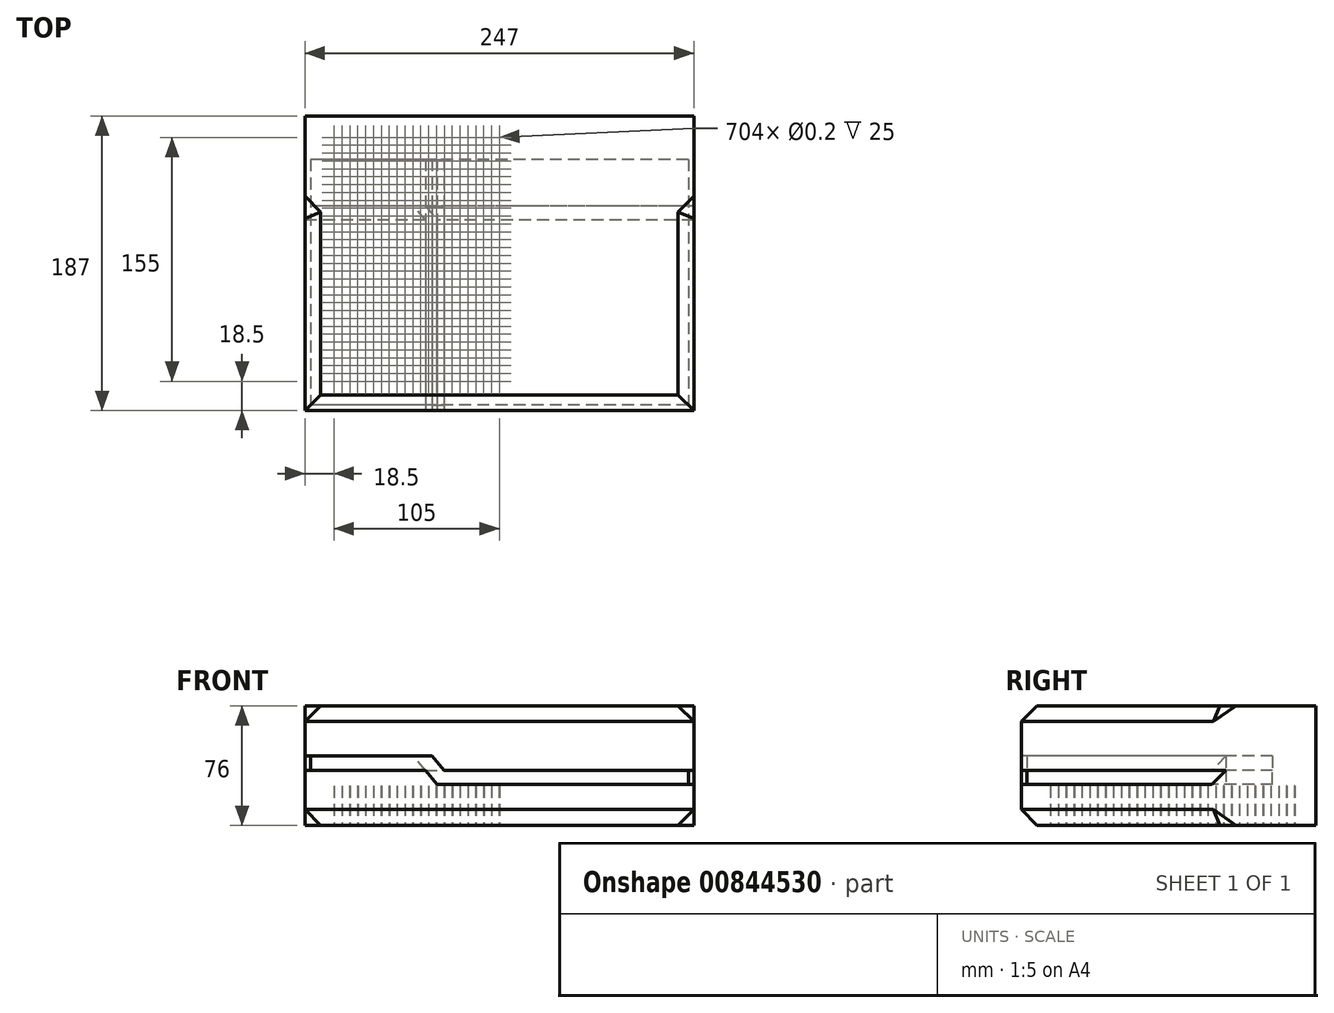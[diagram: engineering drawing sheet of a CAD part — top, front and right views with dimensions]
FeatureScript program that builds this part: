
annotation { "Feature Type Name" : "Feature", "Feature Type Description" : "" }
export const myFeature = defineFeature(function(context is Context, id is Id, definition is map)
    precondition{}
    {
        {
            var Q0;
            Q0=qCreatedBy(makeId("Top.planeOp"),FACE);
            var sketch = newSketch(context, id + "F0", { "sketchPlane" : qUnion([Q0])});
            skLineSegment(sketch, "E0.bottom", {"start": v(123.5, -93.5) * mm, "end": v(-123.5, -93.5) * mm});
            skLineSegment(sketch, "E0.top", {"start": v(123.5, 93.5) * mm, "end": v(-123.5, 93.5) * mm});
            skLineSegment(sketch, "E0.left", {"start": v(123.5, -93.5) * mm, "end": v(123.5, 93.5) * mm});
            skLineSegment(sketch, "E0.right", {"start": v(-123.5, -93.5) * mm, "end": v(-123.5, 93.5) * mm});
            skPoint(sketch, "E0.middle", {"position": v(0, 0) * mm});
            skSolve(sketch);
        }
        {
            var Q0;
            Q0 = qSketchRegion(id + "F0", true);
            extrude(context, id + "F1", {"entities" : qUnion([Q0]), "depth" : 76 * mm, "offsetDistance" : 25 * mm});
        }
        {
            var Q0;
            Q0=makeQuery(id+"F1.opExtrude","CAP_EDGE",EDGE,{"disambiguationData":[OSD([sQuery(id+"F0.wireOp",EDGE,"E0.right")])],"isStart":false});
            var Q1;
            Q1=makeQuery(id+"F1.opExtrude","CAP_EDGE",EDGE,{"disambiguationData":[OSD([sQuery(id+"F0.wireOp",EDGE,"E0.left")])],"isStart":false});
            var Q2;
            Q2=makeQuery(id+"F1.opExtrude","CAP_EDGE",EDGE,{"disambiguationData":[OSD([sQuery(id+"F0.wireOp",EDGE,"E0.right")])],"isStart":true});
            var Q3;
            Q3=makeQuery(id+"F1.opExtrude","CAP_EDGE",EDGE,{"disambiguationData":[OSD([sQuery(id+"F0.wireOp",EDGE,"E0.left")])],"isStart":true});
            var Q4;
            Q4=makeQuery(id+"F1.opExtrude","CAP_EDGE",EDGE,{"disambiguationData":[OSD([sQuery(id+"F0.wireOp",EDGE,"E0.bottom")])],"isStart":false});
            var Q5;
            Q5=makeQuery(id+"F1.opExtrude","CAP_EDGE",EDGE,{"disambiguationData":[OSD([sQuery(id+"F0.wireOp",EDGE,"E0.bottom")])],"isStart":true});
            chamfer(context, id + "F2", {"entities" : qUnion([Q0, Q1, Q2, Q3, Q4, Q5]), "width" : 10 * mm, "tangentPropagation" : true});
        }
        {
            var Q0;
            Q0=makeQuery(id+"F1.opExtrude","SWEPT_FACE",FACE,{"disambiguationData":[OSD([sQuery(id+"F0.wireOp",EDGE,"E0.top")])]});
            var sketch = newSketch(context, id + "F3", { "sketchPlane" : qUnion([Q0])});
            skLineSegment(sketch, "E1", {"start": v(-123.5, 76) * mm, "end": v(-113.5, 76) * mm});
            skLineSegment(sketch, "E2", {"start": v(-113.5, 76) * mm, "end": v(-123.5, 66) * mm});
            skLineSegment(sketch, "E3", {"start": v(-123.5, 66) * mm, "end": v(-123.5, 76) * mm});
            skLineSegment(sketch, "E4", {"start": v(-123.5, 10) * mm, "end": v(-113.5, 0) * mm});
            skLineSegment(sketch, "E5", {"start": v(-113.5, 0) * mm, "end": v(-123.5, 0) * mm});
            skLineSegment(sketch, "E6", {"start": v(-123.5, 0) * mm, "end": v(-123.5, 10) * mm});
            skLineSegment(sketch, "E7", {"start": v(113.5, 76) * mm, "end": v(123.5, 76) * mm});
            skLineSegment(sketch, "E8", {"start": v(123.5, 76) * mm, "end": v(123.5, 66) * mm});
            skLineSegment(sketch, "E9", {"start": v(123.5, 66) * mm, "end": v(113.5, 76) * mm});
            skLineSegment(sketch, "E10", {"start": v(113.5, 0) * mm, "end": v(123.5, 0) * mm});
            skLineSegment(sketch, "E11", {"start": v(123.5, 0) * mm, "end": v(123.5, 10) * mm});
            skLineSegment(sketch, "E12", {"start": v(123.5, 10) * mm, "end": v(113.5, 0) * mm});
            skSolve(sketch);
        }
        {
            var Q0;
            Q0 = qSketchRegion(id + "F3", true);
            extrude(context, id + "F4", {"entities" : qUnion([Q0]), "operationType" : NewBodyOperationType.ADD, "oppositeDirection" : true, "depth" : 75 * mm, "offsetDistance" : 25 * mm});
        }
        {
            var Q0;
            Q0=makeQuery(id+"F4.opExtrude","CAP_EDGE",EDGE,{"disambiguationData":[OSD([sQuery(id+"F3.wireOp",EDGE,"E6")])],"isStart":false});
            var Q1;
            Q1=makeQuery(id+"F4.opExtrude","CAP_EDGE",EDGE,{"disambiguationData":[OSD([sQuery(id+"F3.wireOp",EDGE,"E3")])],"isStart":false});
            var Q2;
            Q2=makeQuery(id+"F4.opExtrude","CAP_EDGE",EDGE,{"disambiguationData":[OSD([sQuery(id+"F3.wireOp",EDGE,"E11")])],"isStart":false});
            var Q3;
            Q3=makeQuery(id+"F4.opExtrude","CAP_EDGE",EDGE,{"disambiguationData":[OSD([sQuery(id+"F3.wireOp",EDGE,"E8")])],"isStart":false});
            chamfer(context, id + "F5", {"entities" : qUnion([Q0, Q1, Q2, Q3]), "width" : 10 * mm, "tangentPropagation" : true});
        }
        {
            var Q0;
            Q0=makeQuery(id+"F5.opChamfer","BLEND_EDGE",EDGE,{"blendedFrom":[makeQuery(id+"F4.opExtrude","CAP_EDGE",EDGE,{"disambiguationData":[OSD([sQuery(id+"F3.wireOp",EDGE,"E6")])],"isStart":false}),makeQuery(id+"F4.boolean.opBoolean","MERGE",FACE,{"derivedFrom":[makeQuery(id+"F1.opExtrude","CAP_FACE",FACE,{"disambiguationData":[OSD([sQuery(id+"F0.wireOp",EDGE,"E0.bottom"),sQuery(id+"F0.wireOp",EDGE,"E0.top"),sQuery(id+"F0.wireOp",EDGE,"E0.left"),sQuery(id+"F0.wireOp",EDGE,"E0.right")])],"isStart":true}),makeQuery(id+"F4.opExtrude","SWEPT_FACE",FACE,{"disambiguationData":[OSD([sQuery(id+"F3.wireOp",EDGE,"E5")])]}),makeQuery(id+"F4.opExtrude","SWEPT_FACE",FACE,{"disambiguationData":[OSD([sQuery(id+"F3.wireOp",EDGE,"E10")])]})]})],"blendedInto":[makeQuery(id+"F4.boolean.opBoolean","MERGE",FACE,{"derivedFrom":[makeQuery(id+"F1.opExtrude","CAP_FACE",FACE,{"disambiguationData":[OSD([sQuery(id+"F0.wireOp",EDGE,"E0.bottom"),sQuery(id+"F0.wireOp",EDGE,"E0.top"),sQuery(id+"F0.wireOp",EDGE,"E0.left"),sQuery(id+"F0.wireOp",EDGE,"E0.right")])],"isStart":true}),makeQuery(id+"F4.opExtrude","SWEPT_FACE",FACE,{"disambiguationData":[OSD([sQuery(id+"F3.wireOp",EDGE,"E5")])]}),makeQuery(id+"F4.opExtrude","SWEPT_FACE",FACE,{"disambiguationData":[OSD([sQuery(id+"F3.wireOp",EDGE,"E10")])]})]})]});
            var Q1;
            Q1=makeQuery(id+"F5.opChamfer","BLEND_EDGE",EDGE,{"blendedFrom":[makeQuery(id+"F4.opExtrude","CAP_EDGE",EDGE,{"disambiguationData":[OSD([sQuery(id+"F3.wireOp",EDGE,"E3")])],"isStart":false}),makeQuery(id+"F4.boolean.opBoolean","MERGE",FACE,{"derivedFrom":[makeQuery(id+"F1.opExtrude","CAP_FACE",FACE,{"disambiguationData":[OSD([sQuery(id+"F0.wireOp",EDGE,"E0.bottom"),sQuery(id+"F0.wireOp",EDGE,"E0.top"),sQuery(id+"F0.wireOp",EDGE,"E0.left"),sQuery(id+"F0.wireOp",EDGE,"E0.right")])],"isStart":false}),makeQuery(id+"F4.opExtrude","SWEPT_FACE",FACE,{"disambiguationData":[OSD([sQuery(id+"F3.wireOp",EDGE,"E1")])]}),makeQuery(id+"F4.opExtrude","SWEPT_FACE",FACE,{"disambiguationData":[OSD([sQuery(id+"F3.wireOp",EDGE,"E7")])]})]})],"blendedInto":[makeQuery(id+"F4.boolean.opBoolean","MERGE",FACE,{"derivedFrom":[makeQuery(id+"F1.opExtrude","CAP_FACE",FACE,{"disambiguationData":[OSD([sQuery(id+"F0.wireOp",EDGE,"E0.bottom"),sQuery(id+"F0.wireOp",EDGE,"E0.top"),sQuery(id+"F0.wireOp",EDGE,"E0.left"),sQuery(id+"F0.wireOp",EDGE,"E0.right")])],"isStart":false}),makeQuery(id+"F4.opExtrude","SWEPT_FACE",FACE,{"disambiguationData":[OSD([sQuery(id+"F3.wireOp",EDGE,"E1")])]}),makeQuery(id+"F4.opExtrude","SWEPT_FACE",FACE,{"disambiguationData":[OSD([sQuery(id+"F3.wireOp",EDGE,"E7")])]})]})]});
            var Q2;
            Q2=makeQuery(id+"F5.opChamfer","BLEND_EDGE",EDGE,{"blendedFrom":[makeQuery(id+"F4.opExtrude","CAP_EDGE",EDGE,{"disambiguationData":[OSD([sQuery(id+"F3.wireOp",EDGE,"E11")])],"isStart":false}),makeQuery(id+"F4.boolean.opBoolean","MERGE",FACE,{"derivedFrom":[makeQuery(id+"F1.opExtrude","CAP_FACE",FACE,{"disambiguationData":[OSD([sQuery(id+"F0.wireOp",EDGE,"E0.bottom"),sQuery(id+"F0.wireOp",EDGE,"E0.top"),sQuery(id+"F0.wireOp",EDGE,"E0.left"),sQuery(id+"F0.wireOp",EDGE,"E0.right")])],"isStart":true}),makeQuery(id+"F4.opExtrude","SWEPT_FACE",FACE,{"disambiguationData":[OSD([sQuery(id+"F3.wireOp",EDGE,"E5")])]}),makeQuery(id+"F4.opExtrude","SWEPT_FACE",FACE,{"disambiguationData":[OSD([sQuery(id+"F3.wireOp",EDGE,"E10")])]})]})],"blendedInto":[makeQuery(id+"F4.boolean.opBoolean","MERGE",FACE,{"derivedFrom":[makeQuery(id+"F1.opExtrude","CAP_FACE",FACE,{"disambiguationData":[OSD([sQuery(id+"F0.wireOp",EDGE,"E0.bottom"),sQuery(id+"F0.wireOp",EDGE,"E0.top"),sQuery(id+"F0.wireOp",EDGE,"E0.left"),sQuery(id+"F0.wireOp",EDGE,"E0.right")])],"isStart":true}),makeQuery(id+"F4.opExtrude","SWEPT_FACE",FACE,{"disambiguationData":[OSD([sQuery(id+"F3.wireOp",EDGE,"E5")])]}),makeQuery(id+"F4.opExtrude","SWEPT_FACE",FACE,{"disambiguationData":[OSD([sQuery(id+"F3.wireOp",EDGE,"E10")])]})]})]});
            var Q3;
            Q3=makeQuery(id+"F5.opChamfer","BLEND_EDGE",EDGE,{"blendedFrom":[makeQuery(id+"F4.opExtrude","CAP_EDGE",EDGE,{"disambiguationData":[OSD([sQuery(id+"F3.wireOp",EDGE,"E8")])],"isStart":false}),makeQuery(id+"F4.boolean.opBoolean","MERGE",FACE,{"derivedFrom":[makeQuery(id+"F1.opExtrude","CAP_FACE",FACE,{"disambiguationData":[OSD([sQuery(id+"F0.wireOp",EDGE,"E0.bottom"),sQuery(id+"F0.wireOp",EDGE,"E0.top"),sQuery(id+"F0.wireOp",EDGE,"E0.left"),sQuery(id+"F0.wireOp",EDGE,"E0.right")])],"isStart":false}),makeQuery(id+"F4.opExtrude","SWEPT_FACE",FACE,{"disambiguationData":[OSD([sQuery(id+"F3.wireOp",EDGE,"E1")])]}),makeQuery(id+"F4.opExtrude","SWEPT_FACE",FACE,{"disambiguationData":[OSD([sQuery(id+"F3.wireOp",EDGE,"E7")])]})]})],"blendedInto":[makeQuery(id+"F4.boolean.opBoolean","MERGE",FACE,{"derivedFrom":[makeQuery(id+"F1.opExtrude","CAP_FACE",FACE,{"disambiguationData":[OSD([sQuery(id+"F0.wireOp",EDGE,"E0.bottom"),sQuery(id+"F0.wireOp",EDGE,"E0.top"),sQuery(id+"F0.wireOp",EDGE,"E0.left"),sQuery(id+"F0.wireOp",EDGE,"E0.right")])],"isStart":false}),makeQuery(id+"F4.opExtrude","SWEPT_FACE",FACE,{"disambiguationData":[OSD([sQuery(id+"F3.wireOp",EDGE,"E1")])]}),makeQuery(id+"F4.opExtrude","SWEPT_FACE",FACE,{"disambiguationData":[OSD([sQuery(id+"F3.wireOp",EDGE,"E7")])]})]})]});
            chamfer(context, id + "F6", {"entities" : qUnion([Q0, Q1, Q2, Q3]), "width" : 10 * mm, "tangentPropagation" : true});
        }
        {
            var Q0;
            Q0=makeQuery(id+"F1.opExtrude","SWEPT_FACE",FACE,{"disambiguationData":[OSD([sQuery(id+"F0.wireOp",EDGE,"E0.bottom")])]});
            var sketch = newSketch(context, id + "F7", { "sketchPlane" : qUnion([Q0])});
            skLineSegment(sketch, "E13", {"start": v(123.5, 10) * mm, "end": v(123.5, 26) * mm});
            skLineSegment(sketch, "E14", {"start": v(123.5, 26) * mm, "end": v(-39.52, 26) * mm});
            skLineSegment(sketch, "E15.0", {"start": v(123.5, 35) * mm, "end": v(-35.3, 35) * mm});
            skLineSegment(sketch, "E16", {"start": v(-47.02, 35) * mm, "end": v(-123.5, 35) * mm});
            skLineSegment(sketch, "E17.0", {"start": v(-42.8, 44) * mm, "end": v(-123.5, 44) * mm});
            skLineSegment(sketch, "E18", {"start": v(-39.52, 26) * mm, "end": v(-47.02, 35) * mm});
            skLineSegment(sketch, "E19", {"start": v(-42.8, 44) * mm, "end": v(-35.3, 35) * mm});
            skLineSegment(sketch, "E20", {"start": v(123.5, 26) * mm, "end": v(123.5, 35) * mm});
            skLineSegment(sketch, "E21", {"start": v(-123.5, 44) * mm, "end": v(-123.5, 35) * mm});
            skSolve(sketch);
        }
        {
            var Q0;
            Q0 = qSketchRegion(id + "F7", true);
            extrude(context, id + "F8", {"entities" : qUnion([Q0]), "operationType" : NewBodyOperationType.REMOVE, "oppositeDirection" : true, "depth" : 130 * mm, "offsetDistance" : 25 * mm});
        }
        {
            var Q0;
            Q0=makeQuery(id+"F8.boolean.opBoolean","COPY",EDGE,{"derivedFrom":makeQuery(id+"F8.opExtrude","CAP_EDGE",EDGE,{"disambiguationData":[OSD([sQuery(id+"F7.wireOp",EDGE,"E16")])],"isStart":false})});
            var Q1;
            Q1=makeQuery(id+"F8.boolean.opBoolean","COPY",EDGE,{"derivedFrom":makeQuery(id+"F8.opExtrude","CAP_EDGE",EDGE,{"disambiguationData":[OSD([sQuery(id+"F7.wireOp",EDGE,"E14")])],"isStart":false})});
            chamfer(context, id + "F9", {"entities" : qUnion([Q0, Q1]), "width" : 9 * mm, "tangentPropagation" : true});
        }
        {
            var Q0;
            Q0=qCreatedBy(makeId("Front.planeOp"),FACE);
            cPlane(context, id + "F10", {"entities" : qUnion([Q0]), "cplaneType" : CPlaneType.OFFSET, "offset" : 90 * mm, "width" : 150 * mm, "height" : 150 * mm});
        }
        {
            var Q0;
            Q0=qCreatedBy(id+"F10.planeOp",FACE);
            var sketch = newSketch(context, id + "F11", { "sketchPlane" : qUnion([Q0])});
            skLineSegment(sketch, "E22", {"start": v(123.5, 26) * mm, "end": v(-39.52, 26) * mm});
            skLineSegment(sketch, "E23.0", {"start": v(123.5, 35) * mm, "end": v(-35.3, 35) * mm});
            skLineSegment(sketch, "E24", {"start": v(-47.02, 35) * mm, "end": v(-123.5, 35) * mm});
            skLineSegment(sketch, "E25.0", {"start": v(-42.8, 44) * mm, "end": v(-123.5, 44) * mm});
            skLineSegment(sketch, "E26", {"start": v(-39.52, 26) * mm, "end": v(-47.02, 35) * mm});
            skLineSegment(sketch, "E27", {"start": v(-42.8, 44) * mm, "end": v(-35.3, 35) * mm});
            skLineSegment(sketch, "E28", {"start": v(123.5, 26) * mm, "end": v(123.5, 35) * mm});
            skLineSegment(sketch, "E29", {"start": v(-123.5, 44) * mm, "end": v(-123.5, 35) * mm});
            skLineSegment(sketch, "E30.0", {"start": v(120, 26) * mm, "end": v(120, 35) * mm});
            skLineSegment(sketch, "E31.0", {"start": v(-120, 44) * mm, "end": v(-120, 35) * mm});
            skSolve(sketch);
        }
        {
            var Q0;
            {var subQ0=sQuery(id+"F11.wireOp",EDGE,"E26");Q0=makeQuery(id+"F11.imprint","IMPRINT",FACE,{"disambiguationData":[TD([[makeQuery(id+"F11.imprint","IMPRINT",EDGE,{"derivedFrom":subQ0}),-1.0]])]});}
            extrude(context, id + "F12", {"entities" : qUnion([Q0]), "oppositeDirection" : true, "depth" : 156 * mm, "offsetDistance" : 25 * mm});
        }
        {
            var Q0;
            Q0=makeQuery(id+"F4.boolean.opBoolean","MERGE",FACE,{"derivedFrom":[makeQuery(id+"F1.opExtrude","CAP_FACE",FACE,{"disambiguationData":[OSD([sQuery(id+"F0.wireOp",EDGE,"E0.bottom"),sQuery(id+"F0.wireOp",EDGE,"E0.top"),sQuery(id+"F0.wireOp",EDGE,"E0.left"),sQuery(id+"F0.wireOp",EDGE,"E0.right")])],"isStart":true}),makeQuery(id+"F4.opExtrude","SWEPT_FACE",FACE,{"disambiguationData":[OSD([sQuery(id+"F3.wireOp",EDGE,"E5")])]}),makeQuery(id+"F4.opExtrude","SWEPT_FACE",FACE,{"disambiguationData":[OSD([sQuery(id+"F3.wireOp",EDGE,"E10")])]})]});
            var sketch = newSketch(context, id + "F13", { "sketchPlane" : qUnion([Q0])});
            skCircle(sketch, "E32", {"center": v(0, 0) * mm, "radius": 0.1 * mm});
            skCircle(sketch, "E33.0.1.0", {"center": v(0, 5) * mm, "radius": 0.1 * mm});
            skCircle(sketch, "E33.0.2.0", {"center": v(0, 10) * mm, "radius": 0.1 * mm});
            skCircle(sketch, "E33.0.3.0", {"center": v(0, 15) * mm, "radius": 0.1 * mm});
            skCircle(sketch, "E33.0.4.0", {"center": v(0, 20) * mm, "radius": 0.1 * mm});
            skCircle(sketch, "E33.0.5.0", {"center": v(0, 25) * mm, "radius": 0.1 * mm});
            skCircle(sketch, "E33.0.6.0", {"center": v(0, 30) * mm, "radius": 0.1 * mm});
            skCircle(sketch, "E33.0.7.0", {"center": v(0, 35) * mm, "radius": 0.1 * mm});
            skCircle(sketch, "E33.0.8.0", {"center": v(0, 40) * mm, "radius": 0.1 * mm});
            skCircle(sketch, "E33.0.9.0", {"center": v(0, 45) * mm, "radius": 0.1 * mm});
            skCircle(sketch, "E33.0.10.0", {"center": v(0, 50) * mm, "radius": 0.1 * mm});
            skCircle(sketch, "E33.0.11.0", {"center": v(0, 55) * mm, "radius": 0.1 * mm});
            skCircle(sketch, "E33.0.12.0", {"center": v(0, 60) * mm, "radius": 0.1 * mm});
            skCircle(sketch, "E33.0.13.0", {"center": v(0, 65) * mm, "radius": 0.1 * mm});
            skCircle(sketch, "E33.0.14.0", {"center": v(0, 70) * mm, "radius": 0.1 * mm});
            skCircle(sketch, "E33.1.0.0", {"center": v(-5, 0) * mm, "radius": 0.1 * mm});
            skCircle(sketch, "E33.1.1.0", {"center": v(-5, 5) * mm, "radius": 0.1 * mm});
            skCircle(sketch, "E33.1.2.0", {"center": v(-5, 10) * mm, "radius": 0.1 * mm});
            skCircle(sketch, "E33.1.3.0", {"center": v(-5, 15) * mm, "radius": 0.1 * mm});
            skCircle(sketch, "E33.1.4.0", {"center": v(-5, 20) * mm, "radius": 0.1 * mm});
            skCircle(sketch, "E33.1.5.0", {"center": v(-5, 25) * mm, "radius": 0.1 * mm});
            skCircle(sketch, "E33.1.6.0", {"center": v(-5, 30) * mm, "radius": 0.1 * mm});
            skCircle(sketch, "E33.1.7.0", {"center": v(-5, 35) * mm, "radius": 0.1 * mm});
            skCircle(sketch, "E33.1.8.0", {"center": v(-5, 40) * mm, "radius": 0.1 * mm});
            skCircle(sketch, "E33.1.9.0", {"center": v(-5, 45) * mm, "radius": 0.1 * mm});
            skCircle(sketch, "E33.1.10.0", {"center": v(-5, 50) * mm, "radius": 0.1 * mm});
            skCircle(sketch, "E33.1.11.0", {"center": v(-5, 55) * mm, "radius": 0.1 * mm});
            skCircle(sketch, "E33.1.12.0", {"center": v(-5, 60) * mm, "radius": 0.1 * mm});
            skCircle(sketch, "E33.1.13.0", {"center": v(-5, 65) * mm, "radius": 0.1 * mm});
            skCircle(sketch, "E33.1.14.0", {"center": v(-5, 70) * mm, "radius": 0.1 * mm});
            skCircle(sketch, "E33.2.0.0", {"center": v(-10, 0) * mm, "radius": 0.1 * mm});
            skCircle(sketch, "E33.2.1.0", {"center": v(-10, 5) * mm, "radius": 0.1 * mm});
            skCircle(sketch, "E33.2.2.0", {"center": v(-10, 10) * mm, "radius": 0.1 * mm});
            skCircle(sketch, "E33.2.3.0", {"center": v(-10, 15) * mm, "radius": 0.1 * mm});
            skCircle(sketch, "E33.2.4.0", {"center": v(-10, 20) * mm, "radius": 0.1 * mm});
            skCircle(sketch, "E33.2.5.0", {"center": v(-10, 25) * mm, "radius": 0.1 * mm});
            skCircle(sketch, "E33.2.6.0", {"center": v(-10, 30) * mm, "radius": 0.1 * mm});
            skCircle(sketch, "E33.2.7.0", {"center": v(-10, 35) * mm, "radius": 0.1 * mm});
            skCircle(sketch, "E33.2.8.0", {"center": v(-10, 40) * mm, "radius": 0.1 * mm});
            skCircle(sketch, "E33.2.9.0", {"center": v(-10, 45) * mm, "radius": 0.1 * mm});
            skCircle(sketch, "E33.2.10.0", {"center": v(-10, 50) * mm, "radius": 0.1 * mm});
            skCircle(sketch, "E33.2.11.0", {"center": v(-10, 55) * mm, "radius": 0.1 * mm});
            skCircle(sketch, "E33.2.12.0", {"center": v(-10, 60) * mm, "radius": 0.1 * mm});
            skCircle(sketch, "E33.2.13.0", {"center": v(-10, 65) * mm, "radius": 0.1 * mm});
            skCircle(sketch, "E33.2.14.0", {"center": v(-10, 70) * mm, "radius": 0.1 * mm});
            skCircle(sketch, "E33.3.0.0", {"center": v(-15, 0) * mm, "radius": 0.1 * mm});
            skCircle(sketch, "E33.3.1.0", {"center": v(-15, 5) * mm, "radius": 0.1 * mm});
            skCircle(sketch, "E33.3.2.0", {"center": v(-15, 10) * mm, "radius": 0.1 * mm});
            skCircle(sketch, "E33.3.3.0", {"center": v(-15, 15) * mm, "radius": 0.1 * mm});
            skCircle(sketch, "E33.3.4.0", {"center": v(-15, 20) * mm, "radius": 0.1 * mm});
            skCircle(sketch, "E33.3.5.0", {"center": v(-15, 25) * mm, "radius": 0.1 * mm});
            skCircle(sketch, "E33.3.6.0", {"center": v(-15, 30) * mm, "radius": 0.1 * mm});
            skCircle(sketch, "E33.3.7.0", {"center": v(-15, 35) * mm, "radius": 0.1 * mm});
            skCircle(sketch, "E33.3.8.0", {"center": v(-15, 40) * mm, "radius": 0.1 * mm});
            skCircle(sketch, "E33.3.9.0", {"center": v(-15, 45) * mm, "radius": 0.1 * mm});
            skCircle(sketch, "E33.3.10.0", {"center": v(-15, 50) * mm, "radius": 0.1 * mm});
            skCircle(sketch, "E33.3.11.0", {"center": v(-15, 55) * mm, "radius": 0.1 * mm});
            skCircle(sketch, "E33.3.12.0", {"center": v(-15, 60) * mm, "radius": 0.1 * mm});
            skCircle(sketch, "E33.3.13.0", {"center": v(-15, 65) * mm, "radius": 0.1 * mm});
            skCircle(sketch, "E33.3.14.0", {"center": v(-15, 70) * mm, "radius": 0.1 * mm});
            skCircle(sketch, "E33.4.0.0", {"center": v(-20, 0) * mm, "radius": 0.1 * mm});
            skCircle(sketch, "E33.4.1.0", {"center": v(-20, 5) * mm, "radius": 0.1 * mm});
            skCircle(sketch, "E33.4.2.0", {"center": v(-20, 10) * mm, "radius": 0.1 * mm});
            skCircle(sketch, "E33.4.3.0", {"center": v(-20, 15) * mm, "radius": 0.1 * mm});
            skCircle(sketch, "E33.4.4.0", {"center": v(-20, 20) * mm, "radius": 0.1 * mm});
            skCircle(sketch, "E33.4.5.0", {"center": v(-20, 25) * mm, "radius": 0.1 * mm});
            skCircle(sketch, "E33.4.6.0", {"center": v(-20, 30) * mm, "radius": 0.1 * mm});
            skCircle(sketch, "E33.4.7.0", {"center": v(-20, 35) * mm, "radius": 0.1 * mm});
            skCircle(sketch, "E33.4.8.0", {"center": v(-20, 40) * mm, "radius": 0.1 * mm});
            skCircle(sketch, "E33.4.9.0", {"center": v(-20, 45) * mm, "radius": 0.1 * mm});
            skCircle(sketch, "E33.4.10.0", {"center": v(-20, 50) * mm, "radius": 0.1 * mm});
            skCircle(sketch, "E33.4.11.0", {"center": v(-20, 55) * mm, "radius": 0.1 * mm});
            skCircle(sketch, "E33.4.12.0", {"center": v(-20, 60) * mm, "radius": 0.1 * mm});
            skCircle(sketch, "E33.4.13.0", {"center": v(-20, 65) * mm, "radius": 0.1 * mm});
            skCircle(sketch, "E33.4.14.0", {"center": v(-20, 70) * mm, "radius": 0.1 * mm});
            skCircle(sketch, "E33.5.0.0", {"center": v(-25, 0) * mm, "radius": 0.1 * mm});
            skCircle(sketch, "E33.5.1.0", {"center": v(-25, 5) * mm, "radius": 0.1 * mm});
            skCircle(sketch, "E33.5.2.0", {"center": v(-25, 10) * mm, "radius": 0.1 * mm});
            skCircle(sketch, "E33.5.3.0", {"center": v(-25, 15) * mm, "radius": 0.1 * mm});
            skCircle(sketch, "E33.5.4.0", {"center": v(-25, 20) * mm, "radius": 0.1 * mm});
            skCircle(sketch, "E33.5.5.0", {"center": v(-25, 25) * mm, "radius": 0.1 * mm});
            skCircle(sketch, "E33.5.6.0", {"center": v(-25, 30) * mm, "radius": 0.1 * mm});
            skCircle(sketch, "E33.5.7.0", {"center": v(-25, 35) * mm, "radius": 0.1 * mm});
            skCircle(sketch, "E33.5.8.0", {"center": v(-25, 40) * mm, "radius": 0.1 * mm});
            skCircle(sketch, "E33.5.9.0", {"center": v(-25, 45) * mm, "radius": 0.1 * mm});
            skCircle(sketch, "E33.5.10.0", {"center": v(-25, 50) * mm, "radius": 0.1 * mm});
            skCircle(sketch, "E33.5.11.0", {"center": v(-25, 55) * mm, "radius": 0.1 * mm});
            skCircle(sketch, "E33.5.12.0", {"center": v(-25, 60) * mm, "radius": 0.1 * mm});
            skCircle(sketch, "E33.5.13.0", {"center": v(-25, 65) * mm, "radius": 0.1 * mm});
            skCircle(sketch, "E33.5.14.0", {"center": v(-25, 70) * mm, "radius": 0.1 * mm});
            skCircle(sketch, "E33.6.0.0", {"center": v(-30, 0) * mm, "radius": 0.1 * mm});
            skCircle(sketch, "E33.6.1.0", {"center": v(-30, 5) * mm, "radius": 0.1 * mm});
            skCircle(sketch, "E33.6.2.0", {"center": v(-30, 10) * mm, "radius": 0.1 * mm});
            skCircle(sketch, "E33.6.3.0", {"center": v(-30, 15) * mm, "radius": 0.1 * mm});
            skCircle(sketch, "E33.6.4.0", {"center": v(-30, 20) * mm, "radius": 0.1 * mm});
            skCircle(sketch, "E33.6.5.0", {"center": v(-30, 25) * mm, "radius": 0.1 * mm});
            skCircle(sketch, "E33.6.6.0", {"center": v(-30, 30) * mm, "radius": 0.1 * mm});
            skCircle(sketch, "E33.6.7.0", {"center": v(-30, 35) * mm, "radius": 0.1 * mm});
            skCircle(sketch, "E33.6.8.0", {"center": v(-30, 40) * mm, "radius": 0.1 * mm});
            skCircle(sketch, "E33.6.9.0", {"center": v(-30, 45) * mm, "radius": 0.1 * mm});
            skCircle(sketch, "E33.6.10.0", {"center": v(-30, 50) * mm, "radius": 0.1 * mm});
            skCircle(sketch, "E33.6.11.0", {"center": v(-30, 55) * mm, "radius": 0.1 * mm});
            skCircle(sketch, "E33.6.12.0", {"center": v(-30, 60) * mm, "radius": 0.1 * mm});
            skCircle(sketch, "E33.6.13.0", {"center": v(-30, 65) * mm, "radius": 0.1 * mm});
            skCircle(sketch, "E33.6.14.0", {"center": v(-30, 70) * mm, "radius": 0.1 * mm});
            skCircle(sketch, "E33.7.0.0", {"center": v(-35, 0) * mm, "radius": 0.1 * mm});
            skCircle(sketch, "E33.7.1.0", {"center": v(-35, 5) * mm, "radius": 0.1 * mm});
            skCircle(sketch, "E33.7.2.0", {"center": v(-35, 10) * mm, "radius": 0.1 * mm});
            skCircle(sketch, "E33.7.3.0", {"center": v(-35, 15) * mm, "radius": 0.1 * mm});
            skCircle(sketch, "E33.7.4.0", {"center": v(-35, 20) * mm, "radius": 0.1 * mm});
            skCircle(sketch, "E33.7.5.0", {"center": v(-35, 25) * mm, "radius": 0.1 * mm});
            skCircle(sketch, "E33.7.6.0", {"center": v(-35, 30) * mm, "radius": 0.1 * mm});
            skCircle(sketch, "E33.7.7.0", {"center": v(-35, 35) * mm, "radius": 0.1 * mm});
            skCircle(sketch, "E33.7.8.0", {"center": v(-35, 40) * mm, "radius": 0.1 * mm});
            skCircle(sketch, "E33.7.9.0", {"center": v(-35, 45) * mm, "radius": 0.1 * mm});
            skCircle(sketch, "E33.7.10.0", {"center": v(-35, 50) * mm, "radius": 0.1 * mm});
            skCircle(sketch, "E33.7.11.0", {"center": v(-35, 55) * mm, "radius": 0.1 * mm});
            skCircle(sketch, "E33.7.12.0", {"center": v(-35, 60) * mm, "radius": 0.1 * mm});
            skCircle(sketch, "E33.7.13.0", {"center": v(-35, 65) * mm, "radius": 0.1 * mm});
            skCircle(sketch, "E33.7.14.0", {"center": v(-35, 70) * mm, "radius": 0.1 * mm});
            skCircle(sketch, "E33.8.0.0", {"center": v(-40, 0) * mm, "radius": 0.1 * mm});
            skCircle(sketch, "E33.8.1.0", {"center": v(-40, 5) * mm, "radius": 0.1 * mm});
            skCircle(sketch, "E33.8.2.0", {"center": v(-40, 10) * mm, "radius": 0.1 * mm});
            skCircle(sketch, "E33.8.3.0", {"center": v(-40, 15) * mm, "radius": 0.1 * mm});
            skCircle(sketch, "E33.8.4.0", {"center": v(-40, 20) * mm, "radius": 0.1 * mm});
            skCircle(sketch, "E33.8.5.0", {"center": v(-40, 25) * mm, "radius": 0.1 * mm});
            skCircle(sketch, "E33.8.6.0", {"center": v(-40, 30) * mm, "radius": 0.1 * mm});
            skCircle(sketch, "E33.8.7.0", {"center": v(-40, 35) * mm, "radius": 0.1 * mm});
            skCircle(sketch, "E33.8.8.0", {"center": v(-40, 40) * mm, "radius": 0.1 * mm});
            skCircle(sketch, "E33.8.9.0", {"center": v(-40, 45) * mm, "radius": 0.1 * mm});
            skCircle(sketch, "E33.8.10.0", {"center": v(-40, 50) * mm, "radius": 0.1 * mm});
            skCircle(sketch, "E33.8.11.0", {"center": v(-40, 55) * mm, "radius": 0.1 * mm});
            skCircle(sketch, "E33.8.12.0", {"center": v(-40, 60) * mm, "radius": 0.1 * mm});
            skCircle(sketch, "E33.8.13.0", {"center": v(-40, 65) * mm, "radius": 0.1 * mm});
            skCircle(sketch, "E33.8.14.0", {"center": v(-40, 70) * mm, "radius": 0.1 * mm});
            skCircle(sketch, "E33.9.0.0", {"center": v(-45, 0) * mm, "radius": 0.1 * mm});
            skCircle(sketch, "E33.9.1.0", {"center": v(-45, 5) * mm, "radius": 0.1 * mm});
            skCircle(sketch, "E33.9.2.0", {"center": v(-45, 10) * mm, "radius": 0.1 * mm});
            skCircle(sketch, "E33.9.3.0", {"center": v(-45, 15) * mm, "radius": 0.1 * mm});
            skCircle(sketch, "E33.9.4.0", {"center": v(-45, 20) * mm, "radius": 0.1 * mm});
            skCircle(sketch, "E33.9.5.0", {"center": v(-45, 25) * mm, "radius": 0.1 * mm});
            skCircle(sketch, "E33.9.6.0", {"center": v(-45, 30) * mm, "radius": 0.1 * mm});
            skCircle(sketch, "E33.9.7.0", {"center": v(-45, 35) * mm, "radius": 0.1 * mm});
            skCircle(sketch, "E33.9.8.0", {"center": v(-45, 40) * mm, "radius": 0.1 * mm});
            skCircle(sketch, "E33.9.9.0", {"center": v(-45, 45) * mm, "radius": 0.1 * mm});
            skCircle(sketch, "E33.9.10.0", {"center": v(-45, 50) * mm, "radius": 0.1 * mm});
            skCircle(sketch, "E33.9.11.0", {"center": v(-45, 55) * mm, "radius": 0.1 * mm});
            skCircle(sketch, "E33.9.12.0", {"center": v(-45, 60) * mm, "radius": 0.1 * mm});
            skCircle(sketch, "E33.9.13.0", {"center": v(-45, 65) * mm, "radius": 0.1 * mm});
            skCircle(sketch, "E33.9.14.0", {"center": v(-45, 70) * mm, "radius": 0.1 * mm});
            skCircle(sketch, "E33.10.0.0", {"center": v(-50, 0) * mm, "radius": 0.1 * mm});
            skCircle(sketch, "E33.10.1.0", {"center": v(-50, 5) * mm, "radius": 0.1 * mm});
            skCircle(sketch, "E33.10.2.0", {"center": v(-50, 10) * mm, "radius": 0.1 * mm});
            skCircle(sketch, "E33.10.3.0", {"center": v(-50, 15) * mm, "radius": 0.1 * mm});
            skCircle(sketch, "E33.10.4.0", {"center": v(-50, 20) * mm, "radius": 0.1 * mm});
            skCircle(sketch, "E33.10.5.0", {"center": v(-50, 25) * mm, "radius": 0.1 * mm});
            skCircle(sketch, "E33.10.6.0", {"center": v(-50, 30) * mm, "radius": 0.1 * mm});
            skCircle(sketch, "E33.10.7.0", {"center": v(-50, 35) * mm, "radius": 0.1 * mm});
            skCircle(sketch, "E33.10.8.0", {"center": v(-50, 40) * mm, "radius": 0.1 * mm});
            skCircle(sketch, "E33.10.9.0", {"center": v(-50, 45) * mm, "radius": 0.1 * mm});
            skCircle(sketch, "E33.10.10.0", {"center": v(-50, 50) * mm, "radius": 0.1 * mm});
            skCircle(sketch, "E33.10.11.0", {"center": v(-50, 55) * mm, "radius": 0.1 * mm});
            skCircle(sketch, "E33.10.12.0", {"center": v(-50, 60) * mm, "radius": 0.1 * mm});
            skCircle(sketch, "E33.10.13.0", {"center": v(-50, 65) * mm, "radius": 0.1 * mm});
            skCircle(sketch, "E33.10.14.0", {"center": v(-50, 70) * mm, "radius": 0.1 * mm});
            skCircle(sketch, "E33.11.0.0", {"center": v(-55, 0) * mm, "radius": 0.1 * mm});
            skCircle(sketch, "E33.11.1.0", {"center": v(-55, 5) * mm, "radius": 0.1 * mm});
            skCircle(sketch, "E33.11.2.0", {"center": v(-55, 10) * mm, "radius": 0.1 * mm});
            skCircle(sketch, "E33.11.3.0", {"center": v(-55, 15) * mm, "radius": 0.1 * mm});
            skCircle(sketch, "E33.11.4.0", {"center": v(-55, 20) * mm, "radius": 0.1 * mm});
            skCircle(sketch, "E33.11.5.0", {"center": v(-55, 25) * mm, "radius": 0.1 * mm});
            skCircle(sketch, "E33.11.6.0", {"center": v(-55, 30) * mm, "radius": 0.1 * mm});
            skCircle(sketch, "E33.11.7.0", {"center": v(-55, 35) * mm, "radius": 0.1 * mm});
            skCircle(sketch, "E33.11.8.0", {"center": v(-55, 40) * mm, "radius": 0.1 * mm});
            skCircle(sketch, "E33.11.9.0", {"center": v(-55, 45) * mm, "radius": 0.1 * mm});
            skCircle(sketch, "E33.11.10.0", {"center": v(-55, 50) * mm, "radius": 0.1 * mm});
            skCircle(sketch, "E33.11.11.0", {"center": v(-55, 55) * mm, "radius": 0.1 * mm});
            skCircle(sketch, "E33.11.12.0", {"center": v(-55, 60) * mm, "radius": 0.1 * mm});
            skCircle(sketch, "E33.11.13.0", {"center": v(-55, 65) * mm, "radius": 0.1 * mm});
            skCircle(sketch, "E33.11.14.0", {"center": v(-55, 70) * mm, "radius": 0.1 * mm});
            skCircle(sketch, "E33.12.0.0", {"center": v(-60, 0) * mm, "radius": 0.1 * mm});
            skCircle(sketch, "E33.12.1.0", {"center": v(-60, 5) * mm, "radius": 0.1 * mm});
            skCircle(sketch, "E33.12.2.0", {"center": v(-60, 10) * mm, "radius": 0.1 * mm});
            skCircle(sketch, "E33.12.3.0", {"center": v(-60, 15) * mm, "radius": 0.1 * mm});
            skCircle(sketch, "E33.12.4.0", {"center": v(-60, 20) * mm, "radius": 0.1 * mm});
            skCircle(sketch, "E33.12.5.0", {"center": v(-60, 25) * mm, "radius": 0.1 * mm});
            skCircle(sketch, "E33.12.6.0", {"center": v(-60, 30) * mm, "radius": 0.1 * mm});
            skCircle(sketch, "E33.12.7.0", {"center": v(-60, 35) * mm, "radius": 0.1 * mm});
            skCircle(sketch, "E33.12.8.0", {"center": v(-60, 40) * mm, "radius": 0.1 * mm});
            skCircle(sketch, "E33.12.9.0", {"center": v(-60, 45) * mm, "radius": 0.1 * mm});
            skCircle(sketch, "E33.12.10.0", {"center": v(-60, 50) * mm, "radius": 0.1 * mm});
            skCircle(sketch, "E33.12.11.0", {"center": v(-60, 55) * mm, "radius": 0.1 * mm});
            skCircle(sketch, "E33.12.12.0", {"center": v(-60, 60) * mm, "radius": 0.1 * mm});
            skCircle(sketch, "E33.12.13.0", {"center": v(-60, 65) * mm, "radius": 0.1 * mm});
            skCircle(sketch, "E33.12.14.0", {"center": v(-60, 70) * mm, "radius": 0.1 * mm});
            skCircle(sketch, "E33.13.0.0", {"center": v(-65, 0) * mm, "radius": 0.1 * mm});
            skCircle(sketch, "E33.13.1.0", {"center": v(-65, 5) * mm, "radius": 0.1 * mm});
            skCircle(sketch, "E33.13.2.0", {"center": v(-65, 10) * mm, "radius": 0.1 * mm});
            skCircle(sketch, "E33.13.3.0", {"center": v(-65, 15) * mm, "radius": 0.1 * mm});
            skCircle(sketch, "E33.13.4.0", {"center": v(-65, 20) * mm, "radius": 0.1 * mm});
            skCircle(sketch, "E33.13.5.0", {"center": v(-65, 25) * mm, "radius": 0.1 * mm});
            skCircle(sketch, "E33.13.6.0", {"center": v(-65, 30) * mm, "radius": 0.1 * mm});
            skCircle(sketch, "E33.13.7.0", {"center": v(-65, 35) * mm, "radius": 0.1 * mm});
            skCircle(sketch, "E33.13.8.0", {"center": v(-65, 40) * mm, "radius": 0.1 * mm});
            skCircle(sketch, "E33.13.9.0", {"center": v(-65, 45) * mm, "radius": 0.1 * mm});
            skCircle(sketch, "E33.13.10.0", {"center": v(-65, 50) * mm, "radius": 0.1 * mm});
            skCircle(sketch, "E33.13.11.0", {"center": v(-65, 55) * mm, "radius": 0.1 * mm});
            skCircle(sketch, "E33.13.12.0", {"center": v(-65, 60) * mm, "radius": 0.1 * mm});
            skCircle(sketch, "E33.13.13.0", {"center": v(-65, 65) * mm, "radius": 0.1 * mm});
            skCircle(sketch, "E33.13.14.0", {"center": v(-65, 70) * mm, "radius": 0.1 * mm});
            skCircle(sketch, "E33.14.0.0", {"center": v(-70, 0) * mm, "radius": 0.1 * mm});
            skCircle(sketch, "E33.14.1.0", {"center": v(-70, 5) * mm, "radius": 0.1 * mm});
            skCircle(sketch, "E33.14.2.0", {"center": v(-70, 10) * mm, "radius": 0.1 * mm});
            skCircle(sketch, "E33.14.3.0", {"center": v(-70, 15) * mm, "radius": 0.1 * mm});
            skCircle(sketch, "E33.14.4.0", {"center": v(-70, 20) * mm, "radius": 0.1 * mm});
            skCircle(sketch, "E33.14.5.0", {"center": v(-70, 25) * mm, "radius": 0.1 * mm});
            skCircle(sketch, "E33.14.6.0", {"center": v(-70, 30) * mm, "radius": 0.1 * mm});
            skCircle(sketch, "E33.14.7.0", {"center": v(-70, 35) * mm, "radius": 0.1 * mm});
            skCircle(sketch, "E33.14.8.0", {"center": v(-70, 40) * mm, "radius": 0.1 * mm});
            skCircle(sketch, "E33.14.9.0", {"center": v(-70, 45) * mm, "radius": 0.1 * mm});
            skCircle(sketch, "E33.14.10.0", {"center": v(-70, 50) * mm, "radius": 0.1 * mm});
            skCircle(sketch, "E33.14.11.0", {"center": v(-70, 55) * mm, "radius": 0.1 * mm});
            skCircle(sketch, "E33.14.12.0", {"center": v(-70, 60) * mm, "radius": 0.1 * mm});
            skCircle(sketch, "E33.14.13.0", {"center": v(-70, 65) * mm, "radius": 0.1 * mm});
            skCircle(sketch, "E33.14.14.0", {"center": v(-70, 70) * mm, "radius": 0.1 * mm});
            skCircle(sketch, "E33.15.0.0", {"center": v(-75, 0) * mm, "radius": 0.1 * mm});
            skCircle(sketch, "E33.15.1.0", {"center": v(-75, 5) * mm, "radius": 0.1 * mm});
            skCircle(sketch, "E33.15.2.0", {"center": v(-75, 10) * mm, "radius": 0.1 * mm});
            skCircle(sketch, "E33.15.3.0", {"center": v(-75, 15) * mm, "radius": 0.1 * mm});
            skCircle(sketch, "E33.15.4.0", {"center": v(-75, 20) * mm, "radius": 0.1 * mm});
            skCircle(sketch, "E33.15.5.0", {"center": v(-75, 25) * mm, "radius": 0.1 * mm});
            skCircle(sketch, "E33.15.6.0", {"center": v(-75, 30) * mm, "radius": 0.1 * mm});
            skCircle(sketch, "E33.15.7.0", {"center": v(-75, 35) * mm, "radius": 0.1 * mm});
            skCircle(sketch, "E33.15.8.0", {"center": v(-75, 40) * mm, "radius": 0.1 * mm});
            skCircle(sketch, "E33.15.9.0", {"center": v(-75, 45) * mm, "radius": 0.1 * mm});
            skCircle(sketch, "E33.15.10.0", {"center": v(-75, 50) * mm, "radius": 0.1 * mm});
            skCircle(sketch, "E33.15.11.0", {"center": v(-75, 55) * mm, "radius": 0.1 * mm});
            skCircle(sketch, "E33.15.12.0", {"center": v(-75, 60) * mm, "radius": 0.1 * mm});
            skCircle(sketch, "E33.15.13.0", {"center": v(-75, 65) * mm, "radius": 0.1 * mm});
            skCircle(sketch, "E33.15.14.0", {"center": v(-75, 70) * mm, "radius": 0.1 * mm});
            skCircle(sketch, "E33.16.0.0", {"center": v(-80, 0) * mm, "radius": 0.1 * mm});
            skCircle(sketch, "E33.16.1.0", {"center": v(-80, 5) * mm, "radius": 0.1 * mm});
            skCircle(sketch, "E33.16.2.0", {"center": v(-80, 10) * mm, "radius": 0.1 * mm});
            skCircle(sketch, "E33.16.3.0", {"center": v(-80, 15) * mm, "radius": 0.1 * mm});
            skCircle(sketch, "E33.16.4.0", {"center": v(-80, 20) * mm, "radius": 0.1 * mm});
            skCircle(sketch, "E33.16.5.0", {"center": v(-80, 25) * mm, "radius": 0.1 * mm});
            skCircle(sketch, "E33.16.6.0", {"center": v(-80, 30) * mm, "radius": 0.1 * mm});
            skCircle(sketch, "E33.16.7.0", {"center": v(-80, 35) * mm, "radius": 0.1 * mm});
            skCircle(sketch, "E33.16.8.0", {"center": v(-80, 40) * mm, "radius": 0.1 * mm});
            skCircle(sketch, "E33.16.9.0", {"center": v(-80, 45) * mm, "radius": 0.1 * mm});
            skCircle(sketch, "E33.16.10.0", {"center": v(-80, 50) * mm, "radius": 0.1 * mm});
            skCircle(sketch, "E33.16.11.0", {"center": v(-80, 55) * mm, "radius": 0.1 * mm});
            skCircle(sketch, "E33.16.12.0", {"center": v(-80, 60) * mm, "radius": 0.1 * mm});
            skCircle(sketch, "E33.16.13.0", {"center": v(-80, 65) * mm, "radius": 0.1 * mm});
            skCircle(sketch, "E33.16.14.0", {"center": v(-80, 70) * mm, "radius": 0.1 * mm});
            skCircle(sketch, "E33.17.0.0", {"center": v(-85, 0) * mm, "radius": 0.1 * mm});
            skCircle(sketch, "E33.17.1.0", {"center": v(-85, 5) * mm, "radius": 0.1 * mm});
            skCircle(sketch, "E33.17.2.0", {"center": v(-85, 10) * mm, "radius": 0.1 * mm});
            skCircle(sketch, "E33.17.3.0", {"center": v(-85, 15) * mm, "radius": 0.1 * mm});
            skCircle(sketch, "E33.17.4.0", {"center": v(-85, 20) * mm, "radius": 0.1 * mm});
            skCircle(sketch, "E33.17.5.0", {"center": v(-85, 25) * mm, "radius": 0.1 * mm});
            skCircle(sketch, "E33.17.6.0", {"center": v(-85, 30) * mm, "radius": 0.1 * mm});
            skCircle(sketch, "E33.17.7.0", {"center": v(-85, 35) * mm, "radius": 0.1 * mm});
            skCircle(sketch, "E33.17.8.0", {"center": v(-85, 40) * mm, "radius": 0.1 * mm});
            skCircle(sketch, "E33.17.9.0", {"center": v(-85, 45) * mm, "radius": 0.1 * mm});
            skCircle(sketch, "E33.17.10.0", {"center": v(-85, 50) * mm, "radius": 0.1 * mm});
            skCircle(sketch, "E33.17.11.0", {"center": v(-85, 55) * mm, "radius": 0.1 * mm});
            skCircle(sketch, "E33.17.12.0", {"center": v(-85, 60) * mm, "radius": 0.1 * mm});
            skCircle(sketch, "E33.17.13.0", {"center": v(-85, 65) * mm, "radius": 0.1 * mm});
            skCircle(sketch, "E33.17.14.0", {"center": v(-85, 70) * mm, "radius": 0.1 * mm});
            skCircle(sketch, "E33.18.0.0", {"center": v(-90, 0) * mm, "radius": 0.1 * mm});
            skCircle(sketch, "E33.18.1.0", {"center": v(-90, 5) * mm, "radius": 0.1 * mm});
            skCircle(sketch, "E33.18.2.0", {"center": v(-90, 10) * mm, "radius": 0.1 * mm});
            skCircle(sketch, "E33.18.3.0", {"center": v(-90, 15) * mm, "radius": 0.1 * mm});
            skCircle(sketch, "E33.18.4.0", {"center": v(-90, 20) * mm, "radius": 0.1 * mm});
            skCircle(sketch, "E33.18.5.0", {"center": v(-90, 25) * mm, "radius": 0.1 * mm});
            skCircle(sketch, "E33.18.6.0", {"center": v(-90, 30) * mm, "radius": 0.1 * mm});
            skCircle(sketch, "E33.18.7.0", {"center": v(-90, 35) * mm, "radius": 0.1 * mm});
            skCircle(sketch, "E33.18.8.0", {"center": v(-90, 40) * mm, "radius": 0.1 * mm});
            skCircle(sketch, "E33.18.9.0", {"center": v(-90, 45) * mm, "radius": 0.1 * mm});
            skCircle(sketch, "E33.18.10.0", {"center": v(-90, 50) * mm, "radius": 0.1 * mm});
            skCircle(sketch, "E33.18.11.0", {"center": v(-90, 55) * mm, "radius": 0.1 * mm});
            skCircle(sketch, "E33.18.12.0", {"center": v(-90, 60) * mm, "radius": 0.1 * mm});
            skCircle(sketch, "E33.18.13.0", {"center": v(-90, 65) * mm, "radius": 0.1 * mm});
            skCircle(sketch, "E33.18.14.0", {"center": v(-90, 70) * mm, "radius": 0.1 * mm});
            skCircle(sketch, "E33.19.0.0", {"center": v(-95, 0) * mm, "radius": 0.1 * mm});
            skCircle(sketch, "E33.19.1.0", {"center": v(-95, 5) * mm, "radius": 0.1 * mm});
            skCircle(sketch, "E33.19.2.0", {"center": v(-95, 10) * mm, "radius": 0.1 * mm});
            skCircle(sketch, "E33.19.3.0", {"center": v(-95, 15) * mm, "radius": 0.1 * mm});
            skCircle(sketch, "E33.19.4.0", {"center": v(-95, 20) * mm, "radius": 0.1 * mm});
            skCircle(sketch, "E33.19.5.0", {"center": v(-95, 25) * mm, "radius": 0.1 * mm});
            skCircle(sketch, "E33.19.6.0", {"center": v(-95, 30) * mm, "radius": 0.1 * mm});
            skCircle(sketch, "E33.19.7.0", {"center": v(-95, 35) * mm, "radius": 0.1 * mm});
            skCircle(sketch, "E33.19.8.0", {"center": v(-95, 40) * mm, "radius": 0.1 * mm});
            skCircle(sketch, "E33.19.9.0", {"center": v(-95, 45) * mm, "radius": 0.1 * mm});
            skCircle(sketch, "E33.19.10.0", {"center": v(-95, 50) * mm, "radius": 0.1 * mm});
            skCircle(sketch, "E33.19.11.0", {"center": v(-95, 55) * mm, "radius": 0.1 * mm});
            skCircle(sketch, "E33.19.12.0", {"center": v(-95, 60) * mm, "radius": 0.1 * mm});
            skCircle(sketch, "E33.19.13.0", {"center": v(-95, 65) * mm, "radius": 0.1 * mm});
            skCircle(sketch, "E33.19.14.0", {"center": v(-95, 70) * mm, "radius": 0.1 * mm});
            skCircle(sketch, "E33.20.0.0", {"center": v(-100, 0) * mm, "radius": 0.1 * mm});
            skCircle(sketch, "E33.20.1.0", {"center": v(-100, 5) * mm, "radius": 0.1 * mm});
            skCircle(sketch, "E33.20.2.0", {"center": v(-100, 10) * mm, "radius": 0.1 * mm});
            skCircle(sketch, "E33.20.3.0", {"center": v(-100, 15) * mm, "radius": 0.1 * mm});
            skCircle(sketch, "E33.20.4.0", {"center": v(-100, 20) * mm, "radius": 0.1 * mm});
            skCircle(sketch, "E33.20.5.0", {"center": v(-100, 25) * mm, "radius": 0.1 * mm});
            skCircle(sketch, "E33.20.6.0", {"center": v(-100, 30) * mm, "radius": 0.1 * mm});
            skCircle(sketch, "E33.20.7.0", {"center": v(-100, 35) * mm, "radius": 0.1 * mm});
            skCircle(sketch, "E33.20.8.0", {"center": v(-100, 40) * mm, "radius": 0.1 * mm});
            skCircle(sketch, "E33.20.9.0", {"center": v(-100, 45) * mm, "radius": 0.1 * mm});
            skCircle(sketch, "E33.20.10.0", {"center": v(-100, 50) * mm, "radius": 0.1 * mm});
            skCircle(sketch, "E33.20.11.0", {"center": v(-100, 55) * mm, "radius": 0.1 * mm});
            skCircle(sketch, "E33.20.12.0", {"center": v(-100, 60) * mm, "radius": 0.1 * mm});
            skCircle(sketch, "E33.20.13.0", {"center": v(-100, 65) * mm, "radius": 0.1 * mm});
            skCircle(sketch, "E33.20.14.0", {"center": v(-100, 70) * mm, "radius": 0.1 * mm});
            skCircle(sketch, "E33.21.0.0", {"center": v(-105, 0) * mm, "radius": 0.1 * mm});
            skCircle(sketch, "E33.21.1.0", {"center": v(-105, 5) * mm, "radius": 0.1 * mm});
            skCircle(sketch, "E33.21.2.0", {"center": v(-105, 10) * mm, "radius": 0.1 * mm});
            skCircle(sketch, "E33.21.3.0", {"center": v(-105, 15) * mm, "radius": 0.1 * mm});
            skCircle(sketch, "E33.21.4.0", {"center": v(-105, 20) * mm, "radius": 0.1 * mm});
            skCircle(sketch, "E33.21.5.0", {"center": v(-105, 25) * mm, "radius": 0.1 * mm});
            skCircle(sketch, "E33.21.6.0", {"center": v(-105, 30) * mm, "radius": 0.1 * mm});
            skCircle(sketch, "E33.21.7.0", {"center": v(-105, 35) * mm, "radius": 0.1 * mm});
            skCircle(sketch, "E33.21.8.0", {"center": v(-105, 40) * mm, "radius": 0.1 * mm});
            skCircle(sketch, "E33.21.9.0", {"center": v(-105, 45) * mm, "radius": 0.1 * mm});
            skCircle(sketch, "E33.21.10.0", {"center": v(-105, 50) * mm, "radius": 0.1 * mm});
            skCircle(sketch, "E33.21.11.0", {"center": v(-105, 55) * mm, "radius": 0.1 * mm});
            skCircle(sketch, "E33.21.12.0", {"center": v(-105, 60) * mm, "radius": 0.1 * mm});
            skCircle(sketch, "E33.21.13.0", {"center": v(-105, 65) * mm, "radius": 0.1 * mm});
            skCircle(sketch, "E33.21.14.0", {"center": v(-105, 70) * mm, "radius": 0.1 * mm});
            skLineSegment(sketch, "E33.direction1", {"start": v(0, 0) * mm, "end": v(-5, 0) * mm, "construction": true});
            skLineSegment(sketch, "E33.direction2", {"start": v(0, 0) * mm, "end": v(0, 5) * mm, "construction": true});
            skCircle(sketch, "E34.0.1.0", {"center": v(-75, -5) * mm, "radius": 0.1 * mm});
            skCircle(sketch, "E34.0.1.1", {"center": v(-10, -5) * mm, "radius": 0.1 * mm});
            skCircle(sketch, "E34.0.1.2", {"center": v(-35, -5) * mm, "radius": 0.1 * mm});
            skCircle(sketch, "E34.0.1.3", {"center": v(-80, -5) * mm, "radius": 0.1 * mm});
            skCircle(sketch, "E34.0.1.4", {"center": v(-20, -5) * mm, "radius": 0.1 * mm});
            skCircle(sketch, "E34.0.1.5", {"center": v(-70, -5) * mm, "radius": 0.1 * mm});
            skCircle(sketch, "E34.0.1.6", {"center": v(-100, -5) * mm, "radius": 0.1 * mm});
            skCircle(sketch, "E34.0.1.7", {"center": v(-85, -5) * mm, "radius": 0.1 * mm});
            skCircle(sketch, "E34.0.1.8", {"center": v(-105, -5) * mm, "radius": 0.1 * mm});
            skCircle(sketch, "E34.0.1.9", {"center": v(-25, -5) * mm, "radius": 0.1 * mm});
            skCircle(sketch, "E34.0.1.10", {"center": v(-95, -5) * mm, "radius": 0.1 * mm});
            skCircle(sketch, "E34.0.1.11", {"center": v(-45, -5) * mm, "radius": 0.1 * mm});
            skCircle(sketch, "E34.0.1.12", {"center": v(-30, -5) * mm, "radius": 0.1 * mm});
            skCircle(sketch, "E34.0.1.13", {"center": v(-40, -5) * mm, "radius": 0.1 * mm});
            skCircle(sketch, "E34.0.1.14", {"center": v(-55, -5) * mm, "radius": 0.1 * mm});
            skCircle(sketch, "E34.0.1.15", {"center": v(-15, -5) * mm, "radius": 0.1 * mm});
            skCircle(sketch, "E34.0.1.16", {"center": v(-60, -5) * mm, "radius": 0.1 * mm});
            skCircle(sketch, "E34.0.1.17", {"center": v(-50, -5) * mm, "radius": 0.1 * mm});
            skCircle(sketch, "E34.0.1.18", {"center": v(-90, -5) * mm, "radius": 0.1 * mm});
            skCircle(sketch, "E34.0.1.19", {"center": v(-5, -5) * mm, "radius": 0.1 * mm});
            skCircle(sketch, "E34.0.1.20", {"center": v(-65, -5) * mm, "radius": 0.1 * mm});
            skLineSegment(sketch, "E34.0.1.21", {"start": v(0, -5) * mm, "end": v(-5, -5) * mm, "construction": true});
            skCircle(sketch, "E34.0.1.22", {"center": v(0, -5) * mm, "radius": 0.1 * mm});
            skCircle(sketch, "E34.0.2.0", {"center": v(-75, -10) * mm, "radius": 0.1 * mm});
            skCircle(sketch, "E34.0.2.1", {"center": v(-10, -10) * mm, "radius": 0.1 * mm});
            skCircle(sketch, "E34.0.2.2", {"center": v(-35, -10) * mm, "radius": 0.1 * mm});
            skCircle(sketch, "E34.0.2.3", {"center": v(-80, -10) * mm, "radius": 0.1 * mm});
            skCircle(sketch, "E34.0.2.4", {"center": v(-20, -10) * mm, "radius": 0.1 * mm});
            skCircle(sketch, "E34.0.2.5", {"center": v(-70, -10) * mm, "radius": 0.1 * mm});
            skCircle(sketch, "E34.0.2.6", {"center": v(-100, -10) * mm, "radius": 0.1 * mm});
            skCircle(sketch, "E34.0.2.7", {"center": v(-85, -10) * mm, "radius": 0.1 * mm});
            skCircle(sketch, "E34.0.2.8", {"center": v(-105, -10) * mm, "radius": 0.1 * mm});
            skCircle(sketch, "E34.0.2.9", {"center": v(-25, -10) * mm, "radius": 0.1 * mm});
            skCircle(sketch, "E34.0.2.10", {"center": v(-95, -10) * mm, "radius": 0.1 * mm});
            skCircle(sketch, "E34.0.2.11", {"center": v(-45, -10) * mm, "radius": 0.1 * mm});
            skCircle(sketch, "E34.0.2.12", {"center": v(-30, -10) * mm, "radius": 0.1 * mm});
            skCircle(sketch, "E34.0.2.13", {"center": v(-40, -10) * mm, "radius": 0.1 * mm});
            skCircle(sketch, "E34.0.2.14", {"center": v(-55, -10) * mm, "radius": 0.1 * mm});
            skCircle(sketch, "E34.0.2.15", {"center": v(-15, -10) * mm, "radius": 0.1 * mm});
            skCircle(sketch, "E34.0.2.16", {"center": v(-60, -10) * mm, "radius": 0.1 * mm});
            skCircle(sketch, "E34.0.2.17", {"center": v(-50, -10) * mm, "radius": 0.1 * mm});
            skCircle(sketch, "E34.0.2.18", {"center": v(-90, -10) * mm, "radius": 0.1 * mm});
            skCircle(sketch, "E34.0.2.19", {"center": v(-5, -10) * mm, "radius": 0.1 * mm});
            skCircle(sketch, "E34.0.2.20", {"center": v(-65, -10) * mm, "radius": 0.1 * mm});
            skLineSegment(sketch, "E34.0.2.21", {"start": v(0, -10) * mm, "end": v(-5, -10) * mm, "construction": true});
            skCircle(sketch, "E34.0.2.22", {"center": v(0, -10) * mm, "radius": 0.1 * mm});
            skCircle(sketch, "E34.0.3.0", {"center": v(-75, -15) * mm, "radius": 0.1 * mm});
            skCircle(sketch, "E34.0.3.1", {"center": v(-10, -15) * mm, "radius": 0.1 * mm});
            skCircle(sketch, "E34.0.3.2", {"center": v(-35, -15) * mm, "radius": 0.1 * mm});
            skCircle(sketch, "E34.0.3.3", {"center": v(-80, -15) * mm, "radius": 0.1 * mm});
            skCircle(sketch, "E34.0.3.4", {"center": v(-20, -15) * mm, "radius": 0.1 * mm});
            skCircle(sketch, "E34.0.3.5", {"center": v(-70, -15) * mm, "radius": 0.1 * mm});
            skCircle(sketch, "E34.0.3.6", {"center": v(-100, -15) * mm, "radius": 0.1 * mm});
            skCircle(sketch, "E34.0.3.7", {"center": v(-85, -15) * mm, "radius": 0.1 * mm});
            skCircle(sketch, "E34.0.3.8", {"center": v(-105, -15) * mm, "radius": 0.1 * mm});
            skCircle(sketch, "E34.0.3.9", {"center": v(-25, -15) * mm, "radius": 0.1 * mm});
            skCircle(sketch, "E34.0.3.10", {"center": v(-95, -15) * mm, "radius": 0.1 * mm});
            skCircle(sketch, "E34.0.3.11", {"center": v(-45, -15) * mm, "radius": 0.1 * mm});
            skCircle(sketch, "E34.0.3.12", {"center": v(-30, -15) * mm, "radius": 0.1 * mm});
            skCircle(sketch, "E34.0.3.13", {"center": v(-40, -15) * mm, "radius": 0.1 * mm});
            skCircle(sketch, "E34.0.3.14", {"center": v(-55, -15) * mm, "radius": 0.1 * mm});
            skCircle(sketch, "E34.0.3.15", {"center": v(-15, -15) * mm, "radius": 0.1 * mm});
            skCircle(sketch, "E34.0.3.16", {"center": v(-60, -15) * mm, "radius": 0.1 * mm});
            skCircle(sketch, "E34.0.3.17", {"center": v(-50, -15) * mm, "radius": 0.1 * mm});
            skCircle(sketch, "E34.0.3.18", {"center": v(-90, -15) * mm, "radius": 0.1 * mm});
            skCircle(sketch, "E34.0.3.19", {"center": v(-5, -15) * mm, "radius": 0.1 * mm});
            skCircle(sketch, "E34.0.3.20", {"center": v(-65, -15) * mm, "radius": 0.1 * mm});
            skLineSegment(sketch, "E34.0.3.21", {"start": v(0, -15) * mm, "end": v(-5, -15) * mm, "construction": true});
            skCircle(sketch, "E34.0.3.22", {"center": v(0, -15) * mm, "radius": 0.1 * mm});
            skCircle(sketch, "E34.0.4.0", {"center": v(-75, -20) * mm, "radius": 0.1 * mm});
            skCircle(sketch, "E34.0.4.1", {"center": v(-10, -20) * mm, "radius": 0.1 * mm});
            skCircle(sketch, "E34.0.4.2", {"center": v(-35, -20) * mm, "radius": 0.1 * mm});
            skCircle(sketch, "E34.0.4.3", {"center": v(-80, -20) * mm, "radius": 0.1 * mm});
            skCircle(sketch, "E34.0.4.4", {"center": v(-20, -20) * mm, "radius": 0.1 * mm});
            skCircle(sketch, "E34.0.4.5", {"center": v(-70, -20) * mm, "radius": 0.1 * mm});
            skCircle(sketch, "E34.0.4.6", {"center": v(-100, -20) * mm, "radius": 0.1 * mm});
            skCircle(sketch, "E34.0.4.7", {"center": v(-85, -20) * mm, "radius": 0.1 * mm});
            skCircle(sketch, "E34.0.4.8", {"center": v(-105, -20) * mm, "radius": 0.1 * mm});
            skCircle(sketch, "E34.0.4.9", {"center": v(-25, -20) * mm, "radius": 0.1 * mm});
            skCircle(sketch, "E34.0.4.10", {"center": v(-95, -20) * mm, "radius": 0.1 * mm});
            skCircle(sketch, "E34.0.4.11", {"center": v(-45, -20) * mm, "radius": 0.1 * mm});
            skCircle(sketch, "E34.0.4.12", {"center": v(-30, -20) * mm, "radius": 0.1 * mm});
            skCircle(sketch, "E34.0.4.13", {"center": v(-40, -20) * mm, "radius": 0.1 * mm});
            skCircle(sketch, "E34.0.4.14", {"center": v(-55, -20) * mm, "radius": 0.1 * mm});
            skCircle(sketch, "E34.0.4.15", {"center": v(-15, -20) * mm, "radius": 0.1 * mm});
            skCircle(sketch, "E34.0.4.16", {"center": v(-60, -20) * mm, "radius": 0.1 * mm});
            skCircle(sketch, "E34.0.4.17", {"center": v(-50, -20) * mm, "radius": 0.1 * mm});
            skCircle(sketch, "E34.0.4.18", {"center": v(-90, -20) * mm, "radius": 0.1 * mm});
            skCircle(sketch, "E34.0.4.19", {"center": v(-5, -20) * mm, "radius": 0.1 * mm});
            skCircle(sketch, "E34.0.4.20", {"center": v(-65, -20) * mm, "radius": 0.1 * mm});
            skLineSegment(sketch, "E34.0.4.21", {"start": v(0, -20) * mm, "end": v(-5, -20) * mm, "construction": true});
            skCircle(sketch, "E34.0.4.22", {"center": v(0, -20) * mm, "radius": 0.1 * mm});
            skCircle(sketch, "E34.0.5.0", {"center": v(-75, -25) * mm, "radius": 0.1 * mm});
            skCircle(sketch, "E34.0.5.1", {"center": v(-10, -25) * mm, "radius": 0.1 * mm});
            skCircle(sketch, "E34.0.5.2", {"center": v(-35, -25) * mm, "radius": 0.1 * mm});
            skCircle(sketch, "E34.0.5.3", {"center": v(-80, -25) * mm, "radius": 0.1 * mm});
            skCircle(sketch, "E34.0.5.4", {"center": v(-20, -25) * mm, "radius": 0.1 * mm});
            skCircle(sketch, "E34.0.5.5", {"center": v(-70, -25) * mm, "radius": 0.1 * mm});
            skCircle(sketch, "E34.0.5.6", {"center": v(-100, -25) * mm, "radius": 0.1 * mm});
            skCircle(sketch, "E34.0.5.7", {"center": v(-85, -25) * mm, "radius": 0.1 * mm});
            skCircle(sketch, "E34.0.5.8", {"center": v(-105, -25) * mm, "radius": 0.1 * mm});
            skCircle(sketch, "E34.0.5.9", {"center": v(-25, -25) * mm, "radius": 0.1 * mm});
            skCircle(sketch, "E34.0.5.10", {"center": v(-95, -25) * mm, "radius": 0.1 * mm});
            skCircle(sketch, "E34.0.5.11", {"center": v(-45, -25) * mm, "radius": 0.1 * mm});
            skCircle(sketch, "E34.0.5.12", {"center": v(-30, -25) * mm, "radius": 0.1 * mm});
            skCircle(sketch, "E34.0.5.13", {"center": v(-40, -25) * mm, "radius": 0.1 * mm});
            skCircle(sketch, "E34.0.5.14", {"center": v(-55, -25) * mm, "radius": 0.1 * mm});
            skCircle(sketch, "E34.0.5.15", {"center": v(-15, -25) * mm, "radius": 0.1 * mm});
            skCircle(sketch, "E34.0.5.16", {"center": v(-60, -25) * mm, "radius": 0.1 * mm});
            skCircle(sketch, "E34.0.5.17", {"center": v(-50, -25) * mm, "radius": 0.1 * mm});
            skCircle(sketch, "E34.0.5.18", {"center": v(-90, -25) * mm, "radius": 0.1 * mm});
            skCircle(sketch, "E34.0.5.19", {"center": v(-5, -25) * mm, "radius": 0.1 * mm});
            skCircle(sketch, "E34.0.5.20", {"center": v(-65, -25) * mm, "radius": 0.1 * mm});
            skLineSegment(sketch, "E34.0.5.21", {"start": v(0, -25) * mm, "end": v(-5, -25) * mm, "construction": true});
            skCircle(sketch, "E34.0.5.22", {"center": v(0, -25) * mm, "radius": 0.1 * mm});
            skCircle(sketch, "E34.0.6.0", {"center": v(-75, -30) * mm, "radius": 0.1 * mm});
            skCircle(sketch, "E34.0.6.1", {"center": v(-10, -30) * mm, "radius": 0.1 * mm});
            skCircle(sketch, "E34.0.6.2", {"center": v(-35, -30) * mm, "radius": 0.1 * mm});
            skCircle(sketch, "E34.0.6.3", {"center": v(-80, -30) * mm, "radius": 0.1 * mm});
            skCircle(sketch, "E34.0.6.4", {"center": v(-20, -30) * mm, "radius": 0.1 * mm});
            skCircle(sketch, "E34.0.6.5", {"center": v(-70, -30) * mm, "radius": 0.1 * mm});
            skCircle(sketch, "E34.0.6.6", {"center": v(-100, -30) * mm, "radius": 0.1 * mm});
            skCircle(sketch, "E34.0.6.7", {"center": v(-85, -30) * mm, "radius": 0.1 * mm});
            skCircle(sketch, "E34.0.6.8", {"center": v(-105, -30) * mm, "radius": 0.1 * mm});
            skCircle(sketch, "E34.0.6.9", {"center": v(-25, -30) * mm, "radius": 0.1 * mm});
            skCircle(sketch, "E34.0.6.10", {"center": v(-95, -30) * mm, "radius": 0.1 * mm});
            skCircle(sketch, "E34.0.6.11", {"center": v(-45, -30) * mm, "radius": 0.1 * mm});
            skCircle(sketch, "E34.0.6.12", {"center": v(-30, -30) * mm, "radius": 0.1 * mm});
            skCircle(sketch, "E34.0.6.13", {"center": v(-40, -30) * mm, "radius": 0.1 * mm});
            skCircle(sketch, "E34.0.6.14", {"center": v(-55, -30) * mm, "radius": 0.1 * mm});
            skCircle(sketch, "E34.0.6.15", {"center": v(-15, -30) * mm, "radius": 0.1 * mm});
            skCircle(sketch, "E34.0.6.16", {"center": v(-60, -30) * mm, "radius": 0.1 * mm});
            skCircle(sketch, "E34.0.6.17", {"center": v(-50, -30) * mm, "radius": 0.1 * mm});
            skCircle(sketch, "E34.0.6.18", {"center": v(-90, -30) * mm, "radius": 0.1 * mm});
            skCircle(sketch, "E34.0.6.19", {"center": v(-5, -30) * mm, "radius": 0.1 * mm});
            skCircle(sketch, "E34.0.6.20", {"center": v(-65, -30) * mm, "radius": 0.1 * mm});
            skLineSegment(sketch, "E34.0.6.21", {"start": v(0, -30) * mm, "end": v(-5, -30) * mm, "construction": true});
            skCircle(sketch, "E34.0.6.22", {"center": v(0, -30) * mm, "radius": 0.1 * mm});
            skCircle(sketch, "E34.0.7.0", {"center": v(-75, -35) * mm, "radius": 0.1 * mm});
            skCircle(sketch, "E34.0.7.1", {"center": v(-10, -35) * mm, "radius": 0.1 * mm});
            skCircle(sketch, "E34.0.7.2", {"center": v(-35, -35) * mm, "radius": 0.1 * mm});
            skCircle(sketch, "E34.0.7.3", {"center": v(-80, -35) * mm, "radius": 0.1 * mm});
            skCircle(sketch, "E34.0.7.4", {"center": v(-20, -35) * mm, "radius": 0.1 * mm});
            skCircle(sketch, "E34.0.7.5", {"center": v(-70, -35) * mm, "radius": 0.1 * mm});
            skCircle(sketch, "E34.0.7.6", {"center": v(-100, -35) * mm, "radius": 0.1 * mm});
            skCircle(sketch, "E34.0.7.7", {"center": v(-85, -35) * mm, "radius": 0.1 * mm});
            skCircle(sketch, "E34.0.7.8", {"center": v(-105, -35) * mm, "radius": 0.1 * mm});
            skCircle(sketch, "E34.0.7.9", {"center": v(-25, -35) * mm, "radius": 0.1 * mm});
            skCircle(sketch, "E34.0.7.10", {"center": v(-95, -35) * mm, "radius": 0.1 * mm});
            skCircle(sketch, "E34.0.7.11", {"center": v(-45, -35) * mm, "radius": 0.1 * mm});
            skCircle(sketch, "E34.0.7.12", {"center": v(-30, -35) * mm, "radius": 0.1 * mm});
            skCircle(sketch, "E34.0.7.13", {"center": v(-40, -35) * mm, "radius": 0.1 * mm});
            skCircle(sketch, "E34.0.7.14", {"center": v(-55, -35) * mm, "radius": 0.1 * mm});
            skCircle(sketch, "E34.0.7.15", {"center": v(-15, -35) * mm, "radius": 0.1 * mm});
            skCircle(sketch, "E34.0.7.16", {"center": v(-60, -35) * mm, "radius": 0.1 * mm});
            skCircle(sketch, "E34.0.7.17", {"center": v(-50, -35) * mm, "radius": 0.1 * mm});
            skCircle(sketch, "E34.0.7.18", {"center": v(-90, -35) * mm, "radius": 0.1 * mm});
            skCircle(sketch, "E34.0.7.19", {"center": v(-5, -35) * mm, "radius": 0.1 * mm});
            skCircle(sketch, "E34.0.7.20", {"center": v(-65, -35) * mm, "radius": 0.1 * mm});
            skLineSegment(sketch, "E34.0.7.21", {"start": v(0, -35) * mm, "end": v(-5, -35) * mm, "construction": true});
            skCircle(sketch, "E34.0.7.22", {"center": v(0, -35) * mm, "radius": 0.1 * mm});
            skCircle(sketch, "E34.0.8.0", {"center": v(-75, -40) * mm, "radius": 0.1 * mm});
            skCircle(sketch, "E34.0.8.1", {"center": v(-10, -40) * mm, "radius": 0.1 * mm});
            skCircle(sketch, "E34.0.8.2", {"center": v(-35, -40) * mm, "radius": 0.1 * mm});
            skCircle(sketch, "E34.0.8.3", {"center": v(-80, -40) * mm, "radius": 0.1 * mm});
            skCircle(sketch, "E34.0.8.4", {"center": v(-20, -40) * mm, "radius": 0.1 * mm});
            skCircle(sketch, "E34.0.8.5", {"center": v(-70, -40) * mm, "radius": 0.1 * mm});
            skCircle(sketch, "E34.0.8.6", {"center": v(-100, -40) * mm, "radius": 0.1 * mm});
            skCircle(sketch, "E34.0.8.7", {"center": v(-85, -40) * mm, "radius": 0.1 * mm});
            skCircle(sketch, "E34.0.8.8", {"center": v(-105, -40) * mm, "radius": 0.1 * mm});
            skCircle(sketch, "E34.0.8.9", {"center": v(-25, -40) * mm, "radius": 0.1 * mm});
            skCircle(sketch, "E34.0.8.10", {"center": v(-95, -40) * mm, "radius": 0.1 * mm});
            skCircle(sketch, "E34.0.8.11", {"center": v(-45, -40) * mm, "radius": 0.1 * mm});
            skCircle(sketch, "E34.0.8.12", {"center": v(-30, -40) * mm, "radius": 0.1 * mm});
            skCircle(sketch, "E34.0.8.13", {"center": v(-40, -40) * mm, "radius": 0.1 * mm});
            skCircle(sketch, "E34.0.8.14", {"center": v(-55, -40) * mm, "radius": 0.1 * mm});
            skCircle(sketch, "E34.0.8.15", {"center": v(-15, -40) * mm, "radius": 0.1 * mm});
            skCircle(sketch, "E34.0.8.16", {"center": v(-60, -40) * mm, "radius": 0.1 * mm});
            skCircle(sketch, "E34.0.8.17", {"center": v(-50, -40) * mm, "radius": 0.1 * mm});
            skCircle(sketch, "E34.0.8.18", {"center": v(-90, -40) * mm, "radius": 0.1 * mm});
            skCircle(sketch, "E34.0.8.19", {"center": v(-5, -40) * mm, "radius": 0.1 * mm});
            skCircle(sketch, "E34.0.8.20", {"center": v(-65, -40) * mm, "radius": 0.1 * mm});
            skLineSegment(sketch, "E34.0.8.21", {"start": v(0, -40) * mm, "end": v(-5, -40) * mm, "construction": true});
            skCircle(sketch, "E34.0.8.22", {"center": v(0, -40) * mm, "radius": 0.1 * mm});
            skCircle(sketch, "E34.0.9.0", {"center": v(-75, -45) * mm, "radius": 0.1 * mm});
            skCircle(sketch, "E34.0.9.1", {"center": v(-10, -45) * mm, "radius": 0.1 * mm});
            skCircle(sketch, "E34.0.9.2", {"center": v(-35, -45) * mm, "radius": 0.1 * mm});
            skCircle(sketch, "E34.0.9.3", {"center": v(-80, -45) * mm, "radius": 0.1 * mm});
            skCircle(sketch, "E34.0.9.4", {"center": v(-20, -45) * mm, "radius": 0.1 * mm});
            skCircle(sketch, "E34.0.9.5", {"center": v(-70, -45) * mm, "radius": 0.1 * mm});
            skCircle(sketch, "E34.0.9.6", {"center": v(-100, -45) * mm, "radius": 0.1 * mm});
            skCircle(sketch, "E34.0.9.7", {"center": v(-85, -45) * mm, "radius": 0.1 * mm});
            skCircle(sketch, "E34.0.9.8", {"center": v(-105, -45) * mm, "radius": 0.1 * mm});
            skCircle(sketch, "E34.0.9.9", {"center": v(-25, -45) * mm, "radius": 0.1 * mm});
            skCircle(sketch, "E34.0.9.10", {"center": v(-95, -45) * mm, "radius": 0.1 * mm});
            skCircle(sketch, "E34.0.9.11", {"center": v(-45, -45) * mm, "radius": 0.1 * mm});
            skCircle(sketch, "E34.0.9.12", {"center": v(-30, -45) * mm, "radius": 0.1 * mm});
            skCircle(sketch, "E34.0.9.13", {"center": v(-40, -45) * mm, "radius": 0.1 * mm});
            skCircle(sketch, "E34.0.9.14", {"center": v(-55, -45) * mm, "radius": 0.1 * mm});
            skCircle(sketch, "E34.0.9.15", {"center": v(-15, -45) * mm, "radius": 0.1 * mm});
            skCircle(sketch, "E34.0.9.16", {"center": v(-60, -45) * mm, "radius": 0.1 * mm});
            skCircle(sketch, "E34.0.9.17", {"center": v(-50, -45) * mm, "radius": 0.1 * mm});
            skCircle(sketch, "E34.0.9.18", {"center": v(-90, -45) * mm, "radius": 0.1 * mm});
            skCircle(sketch, "E34.0.9.19", {"center": v(-5, -45) * mm, "radius": 0.1 * mm});
            skCircle(sketch, "E34.0.9.20", {"center": v(-65, -45) * mm, "radius": 0.1 * mm});
            skLineSegment(sketch, "E34.0.9.21", {"start": v(0, -45) * mm, "end": v(-5, -45) * mm, "construction": true});
            skCircle(sketch, "E34.0.9.22", {"center": v(0, -45) * mm, "radius": 0.1 * mm});
            skCircle(sketch, "E34.0.10.0", {"center": v(-75, -50) * mm, "radius": 0.1 * mm});
            skCircle(sketch, "E34.0.10.1", {"center": v(-10, -50) * mm, "radius": 0.1 * mm});
            skCircle(sketch, "E34.0.10.2", {"center": v(-35, -50) * mm, "radius": 0.1 * mm});
            skCircle(sketch, "E34.0.10.3", {"center": v(-80, -50) * mm, "radius": 0.1 * mm});
            skCircle(sketch, "E34.0.10.4", {"center": v(-20, -50) * mm, "radius": 0.1 * mm});
            skCircle(sketch, "E34.0.10.5", {"center": v(-70, -50) * mm, "radius": 0.1 * mm});
            skCircle(sketch, "E34.0.10.6", {"center": v(-100, -50) * mm, "radius": 0.1 * mm});
            skCircle(sketch, "E34.0.10.7", {"center": v(-85, -50) * mm, "radius": 0.1 * mm});
            skCircle(sketch, "E34.0.10.8", {"center": v(-105, -50) * mm, "radius": 0.1 * mm});
            skCircle(sketch, "E34.0.10.9", {"center": v(-25, -50) * mm, "radius": 0.1 * mm});
            skCircle(sketch, "E34.0.10.10", {"center": v(-95, -50) * mm, "radius": 0.1 * mm});
            skCircle(sketch, "E34.0.10.11", {"center": v(-45, -50) * mm, "radius": 0.1 * mm});
            skCircle(sketch, "E34.0.10.12", {"center": v(-30, -50) * mm, "radius": 0.1 * mm});
            skCircle(sketch, "E34.0.10.13", {"center": v(-40, -50) * mm, "radius": 0.1 * mm});
            skCircle(sketch, "E34.0.10.14", {"center": v(-55, -50) * mm, "radius": 0.1 * mm});
            skCircle(sketch, "E34.0.10.15", {"center": v(-15, -50) * mm, "radius": 0.1 * mm});
            skCircle(sketch, "E34.0.10.16", {"center": v(-60, -50) * mm, "radius": 0.1 * mm});
            skCircle(sketch, "E34.0.10.17", {"center": v(-50, -50) * mm, "radius": 0.1 * mm});
            skCircle(sketch, "E34.0.10.18", {"center": v(-90, -50) * mm, "radius": 0.1 * mm});
            skCircle(sketch, "E34.0.10.19", {"center": v(-5, -50) * mm, "radius": 0.1 * mm});
            skCircle(sketch, "E34.0.10.20", {"center": v(-65, -50) * mm, "radius": 0.1 * mm});
            skLineSegment(sketch, "E34.0.10.21", {"start": v(0, -50) * mm, "end": v(-5, -50) * mm, "construction": true});
            skCircle(sketch, "E34.0.10.22", {"center": v(0, -50) * mm, "radius": 0.1 * mm});
            skCircle(sketch, "E34.0.11.0", {"center": v(-75, -55) * mm, "radius": 0.1 * mm});
            skCircle(sketch, "E34.0.11.1", {"center": v(-10, -55) * mm, "radius": 0.1 * mm});
            skCircle(sketch, "E34.0.11.2", {"center": v(-35, -55) * mm, "radius": 0.1 * mm});
            skCircle(sketch, "E34.0.11.3", {"center": v(-80, -55) * mm, "radius": 0.1 * mm});
            skCircle(sketch, "E34.0.11.4", {"center": v(-20, -55) * mm, "radius": 0.1 * mm});
            skCircle(sketch, "E34.0.11.5", {"center": v(-70, -55) * mm, "radius": 0.1 * mm});
            skCircle(sketch, "E34.0.11.6", {"center": v(-100, -55) * mm, "radius": 0.1 * mm});
            skCircle(sketch, "E34.0.11.7", {"center": v(-85, -55) * mm, "radius": 0.1 * mm});
            skCircle(sketch, "E34.0.11.8", {"center": v(-105, -55) * mm, "radius": 0.1 * mm});
            skCircle(sketch, "E34.0.11.9", {"center": v(-25, -55) * mm, "radius": 0.1 * mm});
            skCircle(sketch, "E34.0.11.10", {"center": v(-95, -55) * mm, "radius": 0.1 * mm});
            skCircle(sketch, "E34.0.11.11", {"center": v(-45, -55) * mm, "radius": 0.1 * mm});
            skCircle(sketch, "E34.0.11.12", {"center": v(-30, -55) * mm, "radius": 0.1 * mm});
            skCircle(sketch, "E34.0.11.13", {"center": v(-40, -55) * mm, "radius": 0.1 * mm});
            skCircle(sketch, "E34.0.11.14", {"center": v(-55, -55) * mm, "radius": 0.1 * mm});
            skCircle(sketch, "E34.0.11.15", {"center": v(-15, -55) * mm, "radius": 0.1 * mm});
            skCircle(sketch, "E34.0.11.16", {"center": v(-60, -55) * mm, "radius": 0.1 * mm});
            skCircle(sketch, "E34.0.11.17", {"center": v(-50, -55) * mm, "radius": 0.1 * mm});
            skCircle(sketch, "E34.0.11.18", {"center": v(-90, -55) * mm, "radius": 0.1 * mm});
            skCircle(sketch, "E34.0.11.19", {"center": v(-5, -55) * mm, "radius": 0.1 * mm});
            skCircle(sketch, "E34.0.11.20", {"center": v(-65, -55) * mm, "radius": 0.1 * mm});
            skLineSegment(sketch, "E34.0.11.21", {"start": v(0, -55) * mm, "end": v(-5, -55) * mm, "construction": true});
            skCircle(sketch, "E34.0.11.22", {"center": v(0, -55) * mm, "radius": 0.1 * mm});
            skCircle(sketch, "E34.0.12.0", {"center": v(-75, -60) * mm, "radius": 0.1 * mm});
            skCircle(sketch, "E34.0.12.1", {"center": v(-10, -60) * mm, "radius": 0.1 * mm});
            skCircle(sketch, "E34.0.12.2", {"center": v(-35, -60) * mm, "radius": 0.1 * mm});
            skCircle(sketch, "E34.0.12.3", {"center": v(-80, -60) * mm, "radius": 0.1 * mm});
            skCircle(sketch, "E34.0.12.4", {"center": v(-20, -60) * mm, "radius": 0.1 * mm});
            skCircle(sketch, "E34.0.12.5", {"center": v(-70, -60) * mm, "radius": 0.1 * mm});
            skCircle(sketch, "E34.0.12.6", {"center": v(-100, -60) * mm, "radius": 0.1 * mm});
            skCircle(sketch, "E34.0.12.7", {"center": v(-85, -60) * mm, "radius": 0.1 * mm});
            skCircle(sketch, "E34.0.12.8", {"center": v(-105, -60) * mm, "radius": 0.1 * mm});
            skCircle(sketch, "E34.0.12.9", {"center": v(-25, -60) * mm, "radius": 0.1 * mm});
            skCircle(sketch, "E34.0.12.10", {"center": v(-95, -60) * mm, "radius": 0.1 * mm});
            skCircle(sketch, "E34.0.12.11", {"center": v(-45, -60) * mm, "radius": 0.1 * mm});
            skCircle(sketch, "E34.0.12.12", {"center": v(-30, -60) * mm, "radius": 0.1 * mm});
            skCircle(sketch, "E34.0.12.13", {"center": v(-40, -60) * mm, "radius": 0.1 * mm});
            skCircle(sketch, "E34.0.12.14", {"center": v(-55, -60) * mm, "radius": 0.1 * mm});
            skCircle(sketch, "E34.0.12.15", {"center": v(-15, -60) * mm, "radius": 0.1 * mm});
            skCircle(sketch, "E34.0.12.16", {"center": v(-60, -60) * mm, "radius": 0.1 * mm});
            skCircle(sketch, "E34.0.12.17", {"center": v(-50, -60) * mm, "radius": 0.1 * mm});
            skCircle(sketch, "E34.0.12.18", {"center": v(-90, -60) * mm, "radius": 0.1 * mm});
            skCircle(sketch, "E34.0.12.19", {"center": v(-5, -60) * mm, "radius": 0.1 * mm});
            skCircle(sketch, "E34.0.12.20", {"center": v(-65, -60) * mm, "radius": 0.1 * mm});
            skLineSegment(sketch, "E34.0.12.21", {"start": v(0, -60) * mm, "end": v(-5, -60) * mm, "construction": true});
            skCircle(sketch, "E34.0.12.22", {"center": v(0, -60) * mm, "radius": 0.1 * mm});
            skCircle(sketch, "E34.0.13.0", {"center": v(-75, -65) * mm, "radius": 0.1 * mm});
            skCircle(sketch, "E34.0.13.1", {"center": v(-10, -65) * mm, "radius": 0.1 * mm});
            skCircle(sketch, "E34.0.13.2", {"center": v(-35, -65) * mm, "radius": 0.1 * mm});
            skCircle(sketch, "E34.0.13.3", {"center": v(-80, -65) * mm, "radius": 0.1 * mm});
            skCircle(sketch, "E34.0.13.4", {"center": v(-20, -65) * mm, "radius": 0.1 * mm});
            skCircle(sketch, "E34.0.13.5", {"center": v(-70, -65) * mm, "radius": 0.1 * mm});
            skCircle(sketch, "E34.0.13.6", {"center": v(-100, -65) * mm, "radius": 0.1 * mm});
            skCircle(sketch, "E34.0.13.7", {"center": v(-85, -65) * mm, "radius": 0.1 * mm});
            skCircle(sketch, "E34.0.13.8", {"center": v(-105, -65) * mm, "radius": 0.1 * mm});
            skCircle(sketch, "E34.0.13.9", {"center": v(-25, -65) * mm, "radius": 0.1 * mm});
            skCircle(sketch, "E34.0.13.10", {"center": v(-95, -65) * mm, "radius": 0.1 * mm});
            skCircle(sketch, "E34.0.13.11", {"center": v(-45, -65) * mm, "radius": 0.1 * mm});
            skCircle(sketch, "E34.0.13.12", {"center": v(-30, -65) * mm, "radius": 0.1 * mm});
            skCircle(sketch, "E34.0.13.13", {"center": v(-40, -65) * mm, "radius": 0.1 * mm});
            skCircle(sketch, "E34.0.13.14", {"center": v(-55, -65) * mm, "radius": 0.1 * mm});
            skCircle(sketch, "E34.0.13.15", {"center": v(-15, -65) * mm, "radius": 0.1 * mm});
            skCircle(sketch, "E34.0.13.16", {"center": v(-60, -65) * mm, "radius": 0.1 * mm});
            skCircle(sketch, "E34.0.13.17", {"center": v(-50, -65) * mm, "radius": 0.1 * mm});
            skCircle(sketch, "E34.0.13.18", {"center": v(-90, -65) * mm, "radius": 0.1 * mm});
            skCircle(sketch, "E34.0.13.19", {"center": v(-5, -65) * mm, "radius": 0.1 * mm});
            skCircle(sketch, "E34.0.13.20", {"center": v(-65, -65) * mm, "radius": 0.1 * mm});
            skLineSegment(sketch, "E34.0.13.21", {"start": v(0, -65) * mm, "end": v(-5, -65) * mm, "construction": true});
            skCircle(sketch, "E34.0.13.22", {"center": v(0, -65) * mm, "radius": 0.1 * mm});
            skCircle(sketch, "E34.0.14.0", {"center": v(-75, -70) * mm, "radius": 0.1 * mm});
            skCircle(sketch, "E34.0.14.1", {"center": v(-10, -70) * mm, "radius": 0.1 * mm});
            skCircle(sketch, "E34.0.14.2", {"center": v(-35, -70) * mm, "radius": 0.1 * mm});
            skCircle(sketch, "E34.0.14.3", {"center": v(-80, -70) * mm, "radius": 0.1 * mm});
            skCircle(sketch, "E34.0.14.4", {"center": v(-20, -70) * mm, "radius": 0.1 * mm});
            skCircle(sketch, "E34.0.14.5", {"center": v(-70, -70) * mm, "radius": 0.1 * mm});
            skCircle(sketch, "E34.0.14.6", {"center": v(-100, -70) * mm, "radius": 0.1 * mm});
            skCircle(sketch, "E34.0.14.7", {"center": v(-85, -70) * mm, "radius": 0.1 * mm});
            skCircle(sketch, "E34.0.14.8", {"center": v(-105, -70) * mm, "radius": 0.1 * mm});
            skCircle(sketch, "E34.0.14.9", {"center": v(-25, -70) * mm, "radius": 0.1 * mm});
            skCircle(sketch, "E34.0.14.10", {"center": v(-95, -70) * mm, "radius": 0.1 * mm});
            skCircle(sketch, "E34.0.14.11", {"center": v(-45, -70) * mm, "radius": 0.1 * mm});
            skCircle(sketch, "E34.0.14.12", {"center": v(-30, -70) * mm, "radius": 0.1 * mm});
            skCircle(sketch, "E34.0.14.13", {"center": v(-40, -70) * mm, "radius": 0.1 * mm});
            skCircle(sketch, "E34.0.14.14", {"center": v(-55, -70) * mm, "radius": 0.1 * mm});
            skCircle(sketch, "E34.0.14.15", {"center": v(-15, -70) * mm, "radius": 0.1 * mm});
            skCircle(sketch, "E34.0.14.16", {"center": v(-60, -70) * mm, "radius": 0.1 * mm});
            skCircle(sketch, "E34.0.14.17", {"center": v(-50, -70) * mm, "radius": 0.1 * mm});
            skCircle(sketch, "E34.0.14.18", {"center": v(-90, -70) * mm, "radius": 0.1 * mm});
            skCircle(sketch, "E34.0.14.19", {"center": v(-5, -70) * mm, "radius": 0.1 * mm});
            skCircle(sketch, "E34.0.14.20", {"center": v(-65, -70) * mm, "radius": 0.1 * mm});
            skLineSegment(sketch, "E34.0.14.21", {"start": v(0, -70) * mm, "end": v(-5, -70) * mm, "construction": true});
            skCircle(sketch, "E34.0.14.22", {"center": v(0, -70) * mm, "radius": 0.1 * mm});
            skCircle(sketch, "E34.0.15.0", {"center": v(-75, -75) * mm, "radius": 0.1 * mm});
            skCircle(sketch, "E34.0.15.1", {"center": v(-10, -75) * mm, "radius": 0.1 * mm});
            skCircle(sketch, "E34.0.15.2", {"center": v(-35, -75) * mm, "radius": 0.1 * mm});
            skCircle(sketch, "E34.0.15.3", {"center": v(-80, -75) * mm, "radius": 0.1 * mm});
            skCircle(sketch, "E34.0.15.4", {"center": v(-20, -75) * mm, "radius": 0.1 * mm});
            skCircle(sketch, "E34.0.15.5", {"center": v(-70, -75) * mm, "radius": 0.1 * mm});
            skCircle(sketch, "E34.0.15.6", {"center": v(-100, -75) * mm, "radius": 0.1 * mm});
            skCircle(sketch, "E34.0.15.7", {"center": v(-85, -75) * mm, "radius": 0.1 * mm});
            skCircle(sketch, "E34.0.15.8", {"center": v(-105, -75) * mm, "radius": 0.1 * mm});
            skCircle(sketch, "E34.0.15.9", {"center": v(-25, -75) * mm, "radius": 0.1 * mm});
            skCircle(sketch, "E34.0.15.10", {"center": v(-95, -75) * mm, "radius": 0.1 * mm});
            skCircle(sketch, "E34.0.15.11", {"center": v(-45, -75) * mm, "radius": 0.1 * mm});
            skCircle(sketch, "E34.0.15.12", {"center": v(-30, -75) * mm, "radius": 0.1 * mm});
            skCircle(sketch, "E34.0.15.13", {"center": v(-40, -75) * mm, "radius": 0.1 * mm});
            skCircle(sketch, "E34.0.15.14", {"center": v(-55, -75) * mm, "radius": 0.1 * mm});
            skCircle(sketch, "E34.0.15.15", {"center": v(-15, -75) * mm, "radius": 0.1 * mm});
            skCircle(sketch, "E34.0.15.16", {"center": v(-60, -75) * mm, "radius": 0.1 * mm});
            skCircle(sketch, "E34.0.15.17", {"center": v(-50, -75) * mm, "radius": 0.1 * mm});
            skCircle(sketch, "E34.0.15.18", {"center": v(-90, -75) * mm, "radius": 0.1 * mm});
            skCircle(sketch, "E34.0.15.19", {"center": v(-5, -75) * mm, "radius": 0.1 * mm});
            skCircle(sketch, "E34.0.15.20", {"center": v(-65, -75) * mm, "radius": 0.1 * mm});
            skLineSegment(sketch, "E34.0.15.21", {"start": v(0, -75) * mm, "end": v(-5, -75) * mm, "construction": true});
            skCircle(sketch, "E34.0.15.22", {"center": v(0, -75) * mm, "radius": 0.1 * mm});
            skCircle(sketch, "E34.0.16.0", {"center": v(-75, -80) * mm, "radius": 0.1 * mm});
            skCircle(sketch, "E34.0.16.1", {"center": v(-10, -80) * mm, "radius": 0.1 * mm});
            skCircle(sketch, "E34.0.16.2", {"center": v(-35, -80) * mm, "radius": 0.1 * mm});
            skCircle(sketch, "E34.0.16.3", {"center": v(-80, -80) * mm, "radius": 0.1 * mm});
            skCircle(sketch, "E34.0.16.4", {"center": v(-20, -80) * mm, "radius": 0.1 * mm});
            skCircle(sketch, "E34.0.16.5", {"center": v(-70, -80) * mm, "radius": 0.1 * mm});
            skCircle(sketch, "E34.0.16.6", {"center": v(-100, -80) * mm, "radius": 0.1 * mm});
            skCircle(sketch, "E34.0.16.7", {"center": v(-85, -80) * mm, "radius": 0.1 * mm});
            skCircle(sketch, "E34.0.16.8", {"center": v(-105, -80) * mm, "radius": 0.1 * mm});
            skCircle(sketch, "E34.0.16.9", {"center": v(-25, -80) * mm, "radius": 0.1 * mm});
            skCircle(sketch, "E34.0.16.10", {"center": v(-95, -80) * mm, "radius": 0.1 * mm});
            skCircle(sketch, "E34.0.16.11", {"center": v(-45, -80) * mm, "radius": 0.1 * mm});
            skCircle(sketch, "E34.0.16.12", {"center": v(-30, -80) * mm, "radius": 0.1 * mm});
            skCircle(sketch, "E34.0.16.13", {"center": v(-40, -80) * mm, "radius": 0.1 * mm});
            skCircle(sketch, "E34.0.16.14", {"center": v(-55, -80) * mm, "radius": 0.1 * mm});
            skCircle(sketch, "E34.0.16.15", {"center": v(-15, -80) * mm, "radius": 0.1 * mm});
            skCircle(sketch, "E34.0.16.16", {"center": v(-60, -80) * mm, "radius": 0.1 * mm});
            skCircle(sketch, "E34.0.16.17", {"center": v(-50, -80) * mm, "radius": 0.1 * mm});
            skCircle(sketch, "E34.0.16.18", {"center": v(-90, -80) * mm, "radius": 0.1 * mm});
            skCircle(sketch, "E34.0.16.19", {"center": v(-5, -80) * mm, "radius": 0.1 * mm});
            skCircle(sketch, "E34.0.16.20", {"center": v(-65, -80) * mm, "radius": 0.1 * mm});
            skLineSegment(sketch, "E34.0.16.21", {"start": v(0, -80) * mm, "end": v(-5, -80) * mm, "construction": true});
            skCircle(sketch, "E34.0.16.22", {"center": v(0, -80) * mm, "radius": 0.1 * mm});
            skLineSegment(sketch, "E34.direction1", {"start": v(-105, 0) * mm, "end": v(-80, 0) * mm, "construction": true});
            skLineSegment(sketch, "E34.direction2", {"start": v(-105, 0) * mm, "end": v(-105, -5) * mm, "construction": true});
            skCircle(sketch, "E35.0.1.0", {"center": v(-75, 75) * mm, "radius": 0.1 * mm});
            skCircle(sketch, "E35.0.1.1", {"center": v(-15, 75) * mm, "radius": 0.1 * mm});
            skCircle(sketch, "E35.0.1.2", {"center": v(-40, 75) * mm, "radius": 0.1 * mm});
            skCircle(sketch, "E35.0.1.3", {"center": v(-25, 75) * mm, "radius": 0.1 * mm});
            skCircle(sketch, "E35.0.1.4", {"center": v(-20, 75) * mm, "radius": 0.1 * mm});
            skCircle(sketch, "E35.0.1.5", {"center": v(-90, 75) * mm, "radius": 0.1 * mm});
            skCircle(sketch, "E35.0.1.6", {"center": v(-50, 75) * mm, "radius": 0.1 * mm});
            skCircle(sketch, "E35.0.1.7", {"center": v(-60, 75) * mm, "radius": 0.1 * mm});
            skCircle(sketch, "E35.0.1.8", {"center": v(-70, 75) * mm, "radius": 0.1 * mm});
            skCircle(sketch, "E35.0.1.9", {"center": v(-105, 75) * mm, "radius": 0.1 * mm});
            skCircle(sketch, "E35.0.1.10", {"center": v(-80, 75) * mm, "radius": 0.1 * mm});
            skCircle(sketch, "E35.0.1.11", {"center": v(-100, 75) * mm, "radius": 0.1 * mm});
            skCircle(sketch, "E35.0.1.12", {"center": v(-45, 75) * mm, "radius": 0.1 * mm});
            skCircle(sketch, "E35.0.1.13", {"center": v(0, 75) * mm, "radius": 0.1 * mm});
            skCircle(sketch, "E35.0.1.14", {"center": v(-65, 75) * mm, "radius": 0.1 * mm});
            skCircle(sketch, "E35.0.1.15", {"center": v(-5, 75) * mm, "radius": 0.1 * mm});
            skCircle(sketch, "E35.0.1.16", {"center": v(-10, 75) * mm, "radius": 0.1 * mm});
            skCircle(sketch, "E35.0.1.17", {"center": v(-30, 75) * mm, "radius": 0.1 * mm});
            skCircle(sketch, "E35.0.1.18", {"center": v(-85, 75) * mm, "radius": 0.1 * mm});
            skCircle(sketch, "E35.0.1.19", {"center": v(-95, 75) * mm, "radius": 0.1 * mm});
            skCircle(sketch, "E35.0.1.20", {"center": v(-35, 75) * mm, "radius": 0.1 * mm});
            skCircle(sketch, "E35.0.1.21", {"center": v(-55, 75) * mm, "radius": 0.1 * mm});
            skLineSegment(sketch, "E35.direction1", {"start": v(-105, 70) * mm, "end": v(-80, 70) * mm, "construction": true});
            skLineSegment(sketch, "E35.direction2", {"start": v(-105, 70) * mm, "end": v(-105, 75) * mm, "construction": true});
            skSolve(sketch);
        }
        {
            var Q0;
            Q0 = qSketchRegion(id + "F13", true);
            extrude(context, id + "F14", {"entities" : qUnion([Q0]), "operationType" : NewBodyOperationType.REMOVE, "oppositeDirection" : true, "depth" : 25 * mm, "offsetDistance" : 25 * mm});
        }
    });
